# Revit family: Rhoss_WinFLOW_ECO
name_source: partatom
category: Attrezzatura meccanica
units: mm (PartAtom-declared; Revit-internal decimal feet)

## family parameters
Basato su piano di lavoro = No
Condiviso = No
Numero OmniClass = 23.75.00.00
Punto di calcolo locali = No
Quota connettore circolare = Usa diametro
Sempre verticale = Sì
Taglio con vuoti quando caricato = No
Tipo di parte = Normale
Titolo OmniClass = Climate Control (HVAC)

## types (30) — shared parameters
C Ref = R454B
COND_IN_Diametro = 76 mm
COND_IN_R1 = 0.00°
COND_IN_R2 = 0.00°
COND_OUT_Diametro = 76 mm
COND_OUT_R1 = 0.00°
COND_OUT_R2 = 0.00°
DS_IN_Diametro = 38 mm  [stored 0.124672 ft]
DS_IN_R1 = 0.00°
DS_IN_R2 = 0.00°
DS_OUT_Diametro = 38 mm  [stored 0.124672 ft]
DS_OUT_R1 = 0.00°
DS_OUT_R2 = 0.00°
D_Main = 2209 mm  [stored 7.24738 ft]
D_W_Idra = 3434 mm  [stored 11.2664 ft]
DistanzaDivisorio = 750 mm  [stored 2.46063 ft]
DivisorioOrizzontale_01 = Sì
EVAP_IN_B = 1680 mm  [stored 5.51181 ft]
EVAP_IN_C = 650 mm  [stored 2.13255 ft]
EVAP_IN_Diametro = 76 mm
EVAP_IN_R1 = 0.00°
EVAP_IN_R2 = 0.00°
EVAP_OUT_B = 1290 mm  [stored 4.23228 ft]
EVAP_OUT_C = 650 mm  [stored 2.13255 ft]
EVAP_OUT_Diametro = 76 mm
EVAP_OUT_R1 = 0.00°
EVAP_OUT_R2 = 0.00°
FREON_IN_R1 = 0.00°
FREON_IN_R2 = 0.00°
FREON_OUT_R1 = 0.00°
FREON_OUT_R2 = 0.00°
H_Main = 1855 mm  [stored 6.08596 ft]
Immagine tipo = <Nessuno>
LogoVisibilita = Sì
LongFeet = Sì
Produttore = Rhoss spa
QE_H = 1666 mm  [stored 5.46588 ft]
QE_Spessore_esterno = 300 mm  [stored 0.984252 ft]
QE_W = 860 mm  [stored 2.82152 ft]
RAL 9018 = RAL 9018
REC_IN_Diametro = 76 mm
REC_IN_R1 = 0.00°
REC_IN_R2 = 0.00°
REC_OUT_Diametro = 76 mm
REC_OUT_R1 = 0.00°
REC_OUT_R2 = 0.00°
RispettoD1 = 1200 mm  [stored 3.93701 ft]
RispettoD2 = 1000 mm  [stored 3.28084 ft]
RispettoD4 = 1000 mm  [stored 3.28084 ft]
RispettoMateriale = BoxRispetto
Rispetto_H_daTerra = 3000 mm  [stored 9.84252 ft]
ShortFeet = No
URL = www.rhoss.com
VisibManiglia = Sì
W_Main = 870 mm  [stored 2.85433 ft]
zero-valued in all types: Prospetto di default, __, ____, _____, ______, _______, pResC (kPa), pResE (kPa)

## per-type parameters (varying)
- TCHETU 4185: COND_IN_A=200 mm  [stored 0.656168 ft]; COND_IN_B=350 mm  [stored 1.14829 ft]; COND_IN_C=150 mm  [stored 0.492126 ft]; COND_IN_R3=0.00°; COND_OUT_A=200 mm  [stored 0.656168 ft]; COND_OUT_B=350 mm  [stored 1.14829 ft]; COND_OUT_C=200 mm  [stored 0.656168 ft]; COND_OUT_R3=0.00°; COP_EN14511_W7W45=0; DS_IN_A=200 mm  [stored 0.656168 ft]; DS_IN_B=475 mm  [stored 1.5584 ft]; DS_IN_C=204 mm  [stored 0.669291 ft]; DS_IN_R3=0.00°; DS_OUT_A=200 mm  [stored 0.656168 ft]; DS_OUT_B=725 mm  [stored 2.37861 ft]; DS_OUT_C=204 mm  [stored 0.669291 ft]; DS_OUT_R3=0.00°; EER_EN14511_W35W7=0; EER_EN14511_tC50W7=0; EVAP_IN_A=200 mm  [stored 0.656168 ft]; EVAP_IN_R3=0.00°; EVAP_OUT_A=200 mm  [stored 0.656168 ft]; EVAP_OUT_R3=0.00°; FREON_IN_A=200 mm  [stored 0.656168 ft]; FREON_IN_B=1290 mm  [stored 4.23228 ft]; FREON_IN_C=220 mm  [stored 0.721785 ft]; FREON_IN_Diametro=22 mm  [stored 0.0721785 ft]; FREON_IN_R3=0.00°; FREON_OUT_A=200 mm  [stored 0.656168 ft]; FREON_OUT_B=1680 mm  [stored 5.51181 ft]; FREON_OUT_C=220 mm  [stored 0.721785 ft]; FREON_OUT_Diametro=35 mm  [stored 0.114829 ft]; FREON_OUT_R3=0.00°; F_Mid_STR6=1699 mm; F_OffSet=491 mm  [stored 1.61089 ft]; Frequency (Hz)=0; Is_STR5=No; Is_STR6=Sì; Lw (dBA)=79; Maximum current (A)=0; Nominal current (A)=0; PF_EN14511_W35W7 (kW)=0; PF_EN14511_tC50W7 (kW)=0; PR_EN14511_W45 (kW)=0; PT_EN14511_W7W45 (kW)=0; Psm_EN14511_W35W7 (kW)=0; QTc (m3/h)=0; Qc (m3/h)=0; Qe (m3/h)=0; Qr (m3/h)=0; REC_IN_A=200 mm  [stored 0.656168 ft]; REC_IN_B=475 mm  [stored 1.5584 ft]; REC_IN_C=220 mm  [stored 0.721785 ft]; REC_IN_R3=0.00°; REC_OUT_A=200 mm  [stored 0.656168 ft]; REC_OUT_B=865 mm  [stored 2.83793 ft]; REC_OUT_C=220 mm  [stored 0.721785 ft]; REC_OUT_R3=0.00°; RispettoD3=3434 mm  [stored 11.2664 ft]; SCOP_EN14825=0; SEER_EN14825=0; Starting current (A)=0; Type=CHILLER; Voltage (V)=0; Weight (kg)=1040; dPTc (kPa)=0; dPc (kPa)=0; dPe (kPa)=0; dPr (kPa)=0; n. poles=0
- TCHETU 4210: COND_IN_A=2209 mm  [stored 7.24738 ft]; COND_IN_B=1290 mm  [stored 4.23228 ft]; COND_IN_C=220 mm  [stored 0.721785 ft]; COND_IN_R3=269.98°; COND_OUT_A=2209 mm  [stored 7.24738 ft]; COND_OUT_B=1680 mm  [stored 5.51181 ft]; COND_OUT_C=220 mm  [stored 0.721785 ft]; COND_OUT_R3=269.98°; COP_EN14511_W7W45=0; DS_IN_A=2209 mm  [stored 7.24738 ft]; DS_IN_B=475 mm  [stored 1.5584 ft]; DS_IN_C=204 mm  [stored 0.669291 ft]; DS_IN_R3=269.98°; DS_OUT_A=2209 mm  [stored 7.24738 ft]; DS_OUT_B=725 mm  [stored 2.37861 ft]; DS_OUT_C=204 mm  [stored 0.669291 ft]; DS_OUT_R3=269.98°; EER_EN14511_W35W7=4.62; EER_EN14511_tC50W7=0; EVAP_IN_A=2209 mm  [stored 7.24738 ft]; EVAP_IN_R3=269.98°; EVAP_OUT_A=2209 mm  [stored 7.24738 ft]; EVAP_OUT_R3=269.98°; FREON_IN_A=200 mm  [stored 0.656168 ft]; FREON_IN_B=300 mm  [stored 0.984252 ft]; FREON_IN_C=150 mm  [stored 0.492126 ft]; FREON_IN_Diametro=22 mm  [stored 0.0721785 ft]; FREON_IN_R3=0.00°; FREON_OUT_A=200 mm  [stored 0.656168 ft]; FREON_OUT_B=300 mm  [stored 0.984252 ft]; FREON_OUT_C=200 mm  [stored 0.656168 ft]; FREON_OUT_Diametro=35 mm  [stored 0.114829 ft]; FREON_OUT_R3=0.00°; F_Mid_STR6=795 mm  [stored 2.60827 ft]; F_OffSet=255 mm  [stored 0.836614 ft]; Frequency (Hz)=50; Is_STR5=Sì; Is_STR6=No; Lw (dBA)=79; Maximum current (A)=128.8; Nominal current (A)=81; PF_EN14511_W35W7 (kW)=209; PF_EN14511_tC50W7 (kW)=0; PR_EN14511_W45 (kW)=0; PT_EN14511_W7W45 (kW)=0; Psm_EN14511_W35W7 (kW)=251.4; QTc (m3/h)=0; Qc (m3/h)=43.2; Qe (m3/h)=36; Qr (m3/h)=0; REC_IN_A=2209 mm  [stored 7.24738 ft]; REC_IN_B=475 mm  [stored 1.5584 ft]; REC_IN_C=220 mm  [stored 0.721785 ft]; REC_IN_R3=269.98°; REC_OUT_A=2209 mm  [stored 7.24738 ft]; REC_OUT_B=865 mm  [stored 2.83793 ft]; REC_OUT_C=220 mm  [stored 0.721785 ft]; REC_OUT_R3=269.98°; RispettoD3=2209 mm  [stored 7.24738 ft]; SCOP_EN14825=0; SEER_EN14825=6.36; Starting current (A)=302.4; Type=CHILLER; Voltage (V)=400; Weight (kg)=1105; dPTc (kPa)=0; dPc (kPa)=49; dPe (kPa)=34; dPr (kPa)=0; n. poles=3+N
- TCHETU 4240: COND_IN_A=2209 mm  [stored 7.24738 ft]; COND_IN_B=1290 mm  [stored 4.23228 ft]; COND_IN_C=220 mm  [stored 0.721785 ft]; COND_IN_R3=269.98°; COND_OUT_A=2209 mm  [stored 7.24738 ft]; COND_OUT_B=1680 mm  [stored 5.51181 ft]; COND_OUT_C=220 mm  [stored 0.721785 ft]; COND_OUT_R3=269.98°; COP_EN14511_W7W45=0; DS_IN_A=2209 mm  [stored 7.24738 ft]; DS_IN_B=475 mm  [stored 1.5584 ft]; DS_IN_C=204 mm  [stored 0.669291 ft]; DS_IN_R3=269.98°; DS_OUT_A=2209 mm  [stored 7.24738 ft]; DS_OUT_B=725 mm  [stored 2.37861 ft]; DS_OUT_C=204 mm  [stored 0.669291 ft]; DS_OUT_R3=269.98°; EER_EN14511_W35W7=4.63; EER_EN14511_tC50W7=0; EVAP_IN_A=2209 mm  [stored 7.24738 ft]; EVAP_IN_R3=269.98°; EVAP_OUT_A=2209 mm  [stored 7.24738 ft]; EVAP_OUT_R3=269.98°; FREON_IN_A=200 mm  [stored 0.656168 ft]; FREON_IN_B=300 mm  [stored 0.984252 ft]; FREON_IN_C=150 mm  [stored 0.492126 ft]; FREON_IN_Diametro=22 mm  [stored 0.0721785 ft]; FREON_IN_R3=0.00°; FREON_OUT_A=200 mm  [stored 0.656168 ft]; FREON_OUT_B=300 mm  [stored 0.984252 ft]; FREON_OUT_C=200 mm  [stored 0.656168 ft]; FREON_OUT_Diametro=35 mm  [stored 0.114829 ft]; FREON_OUT_R3=0.00°; F_Mid_STR6=795 mm  [stored 2.60827 ft]; F_OffSet=255 mm  [stored 0.836614 ft]; Frequency (Hz)=50; Is_STR5=Sì; Is_STR6=No; Lw (dBA)=80; Maximum current (A)=149.6; Nominal current (A)=94.4; PF_EN14511_W35W7 (kW)=236.3; PF_EN14511_tC50W7 (kW)=0; PR_EN14511_W45 (kW)=0; PT_EN14511_W7W45 (kW)=0; Psm_EN14511_W35W7 (kW)=284.4; QTc (m3/h)=0; Qc (m3/h)=48.9; Qe (m3/h)=40.7; Qr (m3/h)=0; REC_IN_A=2209 mm  [stored 7.24738 ft]; REC_IN_B=475 mm  [stored 1.5584 ft]; REC_IN_C=220 mm  [stored 0.721785 ft]; REC_IN_R3=269.98°; REC_OUT_A=2209 mm  [stored 7.24738 ft]; REC_OUT_B=865 mm  [stored 2.83793 ft]; REC_OUT_C=220 mm  [stored 0.721785 ft]; REC_OUT_R3=269.98°; RispettoD3=2209 mm  [stored 7.24738 ft]; SCOP_EN14825=0; SEER_EN14825=6.5; Starting current (A)=323.2; Type=CHILLER; Voltage (V)=400; Weight (kg)=1140; dPTc (kPa)=0; dPc (kPa)=42; dPe (kPa)=29; dPr (kPa)=0; n. poles=3+N
- TCHETU 4275: COND_IN_A=2209 mm  [stored 7.24738 ft]; COND_IN_B=1290 mm  [stored 4.23228 ft]; COND_IN_C=220 mm  [stored 0.721785 ft]; COND_IN_R3=269.98°; COND_OUT_A=2209 mm  [stored 7.24738 ft]; COND_OUT_B=1680 mm  [stored 5.51181 ft]; COND_OUT_C=220 mm  [stored 0.721785 ft]; COND_OUT_R3=269.98°; COP_EN14511_W7W45=0; DS_IN_A=2209 mm  [stored 7.24738 ft]; DS_IN_B=475 mm  [stored 1.5584 ft]; DS_IN_C=204 mm  [stored 0.669291 ft]; DS_IN_R3=269.98°; DS_OUT_A=2209 mm  [stored 7.24738 ft]; DS_OUT_B=725 mm  [stored 2.37861 ft]; DS_OUT_C=204 mm  [stored 0.669291 ft]; DS_OUT_R3=269.98°; EER_EN14511_W35W7=4.59; EER_EN14511_tC50W7=0; EVAP_IN_A=2209 mm  [stored 7.24738 ft]; EVAP_IN_R3=269.98°; EVAP_OUT_A=2209 mm  [stored 7.24738 ft]; EVAP_OUT_R3=269.98°; FREON_IN_A=200 mm  [stored 0.656168 ft]; FREON_IN_B=300 mm  [stored 0.984252 ft]; FREON_IN_C=150 mm  [stored 0.492126 ft]; FREON_IN_Diametro=22 mm  [stored 0.0721785 ft]; FREON_IN_R3=0.00°; FREON_OUT_A=200 mm  [stored 0.656168 ft]; FREON_OUT_B=300 mm  [stored 0.984252 ft]; FREON_OUT_C=200 mm  [stored 0.656168 ft]; FREON_OUT_Diametro=35 mm  [stored 0.114829 ft]; FREON_OUT_R3=0.00°; F_Mid_STR6=795 mm  [stored 2.60827 ft]; F_OffSet=255 mm  [stored 0.836614 ft]; Frequency (Hz)=50; Is_STR5=Sì; Is_STR6=No; Lw (dBA)=81; Maximum current (A)=166.4; Nominal current (A)=97.3; PF_EN14511_W35W7 (kW)=267.9; PF_EN14511_tC50W7 (kW)=0; PR_EN14511_W45 (kW)=0; PT_EN14511_W7W45 (kW)=0; Psm_EN14511_W35W7 (kW)=322.5; QTc (m3/h)=0; Qc (m3/h)=55.5; Qe (m3/h)=46.1; Qr (m3/h)=0; REC_IN_A=2209 mm  [stored 7.24738 ft]; REC_IN_B=475 mm  [stored 1.5584 ft]; REC_IN_C=220 mm  [stored 0.721785 ft]; REC_IN_R3=269.98°; REC_OUT_A=2209 mm  [stored 7.24738 ft]; REC_OUT_B=865 mm  [stored 2.83793 ft]; REC_OUT_C=220 mm  [stored 0.721785 ft]; REC_OUT_R3=269.98°; RispettoD3=2209 mm  [stored 7.24738 ft]; SCOP_EN14825=0; SEER_EN14825=6.49; Starting current (A)=330.6; Type=CHILLER; Voltage (V)=400; Weight (kg)=1310; dPTc (kPa)=0; dPc (kPa)=55; dPe (kPa)=38; dPr (kPa)=0; n. poles=3+N
- TCHETU 4305: COND_IN_A=2209 mm  [stored 7.24738 ft]; COND_IN_B=1290 mm  [stored 4.23228 ft]; COND_IN_C=220 mm  [stored 0.721785 ft]; COND_IN_R3=269.98°; COND_OUT_A=2209 mm  [stored 7.24738 ft]; COND_OUT_B=1680 mm  [stored 5.51181 ft]; COND_OUT_C=220 mm  [stored 0.721785 ft]; COND_OUT_R3=269.98°; COP_EN14511_W7W45=0; DS_IN_A=2209 mm  [stored 7.24738 ft]; DS_IN_B=475 mm  [stored 1.5584 ft]; DS_IN_C=204 mm  [stored 0.669291 ft]; DS_IN_R3=269.98°; DS_OUT_A=2209 mm  [stored 7.24738 ft]; DS_OUT_B=725 mm  [stored 2.37861 ft]; DS_OUT_C=204 mm  [stored 0.669291 ft]; DS_OUT_R3=269.98°; EER_EN14511_W35W7=4.54; EER_EN14511_tC50W7=0; EVAP_IN_A=2209 mm  [stored 7.24738 ft]; EVAP_IN_R3=269.98°; EVAP_OUT_A=2209 mm  [stored 7.24738 ft]; EVAP_OUT_R3=269.98°; FREON_IN_A=200 mm  [stored 0.656168 ft]; FREON_IN_B=300 mm  [stored 0.984252 ft]; FREON_IN_C=150 mm  [stored 0.492126 ft]; FREON_IN_Diametro=22 mm  [stored 0.0721785 ft]; FREON_IN_R3=0.00°; FREON_OUT_A=200 mm  [stored 0.656168 ft]; FREON_OUT_B=300 mm  [stored 0.984252 ft]; FREON_OUT_C=200 mm  [stored 0.656168 ft]; FREON_OUT_Diametro=35 mm  [stored 0.114829 ft]; FREON_OUT_R3=0.00°; F_Mid_STR6=795 mm  [stored 2.60827 ft]; F_OffSet=255 mm  [stored 0.836614 ft]; Frequency (Hz)=50; Is_STR5=Sì; Is_STR6=No; Lw (dBA)=83; Maximum current (A)=183.2; Nominal current (A)=100.4; PF_EN14511_W35W7 (kW)=299.1; PF_EN14511_tC50W7 (kW)=0; PR_EN14511_W45 (kW)=0; PT_EN14511_W7W45 (kW)=0; Psm_EN14511_W35W7 (kW)=360.4; QTc (m3/h)=0; Qc (m3/h)=62; Qe (m3/h)=51.5; Qr (m3/h)=0; REC_IN_A=2209 mm  [stored 7.24738 ft]; REC_IN_B=475 mm  [stored 1.5584 ft]; REC_IN_C=220 mm  [stored 0.721785 ft]; REC_IN_R3=269.98°; REC_OUT_A=2209 mm  [stored 7.24738 ft]; REC_OUT_B=865 mm  [stored 2.83793 ft]; REC_OUT_C=220 mm  [stored 0.721785 ft]; REC_OUT_R3=269.98°; RispettoD3=2209 mm  [stored 7.24738 ft]; SCOP_EN14825=0; SEER_EN14825=6.56; Starting current (A)=347.4; Type=CHILLER; Voltage (V)=400; Weight (kg)=1455; dPTc (kPa)=0; dPc (kPa)=68; dPe (kPa)=47; dPr (kPa)=0; n. poles=3+N
- TCHETU 4350: COND_IN_A=2209 mm  [stored 7.24738 ft]; COND_IN_B=1290 mm  [stored 4.23228 ft]; COND_IN_C=220 mm  [stored 0.721785 ft]; COND_IN_R3=269.98°; COND_OUT_A=2209 mm  [stored 7.24738 ft]; COND_OUT_B=1680 mm  [stored 5.51181 ft]; COND_OUT_C=220 mm  [stored 0.721785 ft]; COND_OUT_R3=269.98°; COP_EN14511_W7W45=0; DS_IN_A=2209 mm  [stored 7.24738 ft]; DS_IN_B=475 mm  [stored 1.5584 ft]; DS_IN_C=204 mm  [stored 0.669291 ft]; DS_IN_R3=269.98°; DS_OUT_A=2209 mm  [stored 7.24738 ft]; DS_OUT_B=725 mm  [stored 2.37861 ft]; DS_OUT_C=204 mm  [stored 0.669291 ft]; DS_OUT_R3=269.98°; EER_EN14511_W35W7=4.54; EER_EN14511_tC50W7=0; EVAP_IN_A=2209 mm  [stored 7.24738 ft]; EVAP_IN_R3=269.98°; EVAP_OUT_A=2209 mm  [stored 7.24738 ft]; EVAP_OUT_R3=269.98°; FREON_IN_A=200 mm  [stored 0.656168 ft]; FREON_IN_B=300 mm  [stored 0.984252 ft]; FREON_IN_C=150 mm  [stored 0.492126 ft]; FREON_IN_Diametro=22 mm  [stored 0.0721785 ft]; FREON_IN_R3=0.00°; FREON_OUT_A=200 mm  [stored 0.656168 ft]; FREON_OUT_B=300 mm  [stored 0.984252 ft]; FREON_OUT_C=200 mm  [stored 0.656168 ft]; FREON_OUT_Diametro=35 mm  [stored 0.114829 ft]; FREON_OUT_R3=0.00°; F_Mid_STR6=795 mm  [stored 2.60827 ft]; F_OffSet=255 mm  [stored 0.836614 ft]; Frequency (Hz)=50; Is_STR5=Sì; Is_STR6=No; Lw (dBA)=84; Maximum current (A)=216.4; Nominal current (A)=125; PF_EN14511_W35W7 (kW)=344; PF_EN14511_tC50W7 (kW)=0; PR_EN14511_W45 (kW)=0; PT_EN14511_W7W45 (kW)=0; Psm_EN14511_W35W7 (kW)=414.6; QTc (m3/h)=0; Qc (m3/h)=71.3; Qe (m3/h)=59.2; Qr (m3/h)=0; REC_IN_A=2209 mm  [stored 7.24738 ft]; REC_IN_B=475 mm  [stored 1.5584 ft]; REC_IN_C=220 mm  [stored 0.721785 ft]; REC_IN_R3=269.98°; REC_OUT_A=2209 mm  [stored 7.24738 ft]; REC_OUT_B=865 mm  [stored 2.83793 ft]; REC_OUT_C=220 mm  [stored 0.721785 ft]; REC_OUT_R3=269.98°; RispettoD3=2209 mm  [stored 7.24738 ft]; SCOP_EN14825=0; SEER_EN14825=6.54; Starting current (A)=480; Type=CHILLER; Voltage (V)=400; Weight (kg)=1515; dPTc (kPa)=0; dPc (kPa)=64; dPe (kPa)=44; dPr (kPa)=0; n. poles=3+N
- TCHETU 4395: COND_IN_A=2209 mm  [stored 7.24738 ft]; COND_IN_B=1290 mm  [stored 4.23228 ft]; COND_IN_C=220 mm  [stored 0.721785 ft]; COND_IN_R3=269.98°; COND_OUT_A=2209 mm  [stored 7.24738 ft]; COND_OUT_B=1680 mm  [stored 5.51181 ft]; COND_OUT_C=220 mm  [stored 0.721785 ft]; COND_OUT_R3=269.98°; COP_EN14511_W7W45=0; DS_IN_A=2209 mm  [stored 7.24738 ft]; DS_IN_B=475 mm  [stored 1.5584 ft]; DS_IN_C=204 mm  [stored 0.669291 ft]; DS_IN_R3=269.98°; DS_OUT_A=2209 mm  [stored 7.24738 ft]; DS_OUT_B=725 mm  [stored 2.37861 ft]; DS_OUT_C=204 mm  [stored 0.669291 ft]; DS_OUT_R3=269.98°; EER_EN14511_W35W7=4.44; EER_EN14511_tC50W7=0; EVAP_IN_A=2209 mm  [stored 7.24738 ft]; EVAP_IN_R3=269.98°; EVAP_OUT_A=2209 mm  [stored 7.24738 ft]; EVAP_OUT_R3=269.98°; FREON_IN_A=200 mm  [stored 0.656168 ft]; FREON_IN_B=300 mm  [stored 0.984252 ft]; FREON_IN_C=150 mm  [stored 0.492126 ft]; FREON_IN_Diametro=22 mm  [stored 0.0721785 ft]; FREON_IN_R3=0.00°; FREON_OUT_A=200 mm  [stored 0.656168 ft]; FREON_OUT_B=300 mm  [stored 0.984252 ft]; FREON_OUT_C=200 mm  [stored 0.656168 ft]; FREON_OUT_Diametro=35 mm  [stored 0.114829 ft]; FREON_OUT_R3=0.00°; F_Mid_STR6=795 mm  [stored 2.60827 ft]; F_OffSet=255 mm  [stored 0.836614 ft]; Frequency (Hz)=50; Is_STR5=Sì; Is_STR6=No; Lw (dBA)=85; Maximum current (A)=249.6; Nominal current (A)=151.2; PF_EN14511_W35W7 (kW)=387.6; PF_EN14511_tC50W7 (kW)=0; PR_EN14511_W45 (kW)=0; PT_EN14511_W7W45 (kW)=0; Psm_EN14511_W35W7 (kW)=468.5; QTc (m3/h)=0; Qc (m3/h)=80.6; Qe (m3/h)=66.8; Qr (m3/h)=0; REC_IN_A=2209 mm  [stored 7.24738 ft]; REC_IN_B=475 mm  [stored 1.5584 ft]; REC_IN_C=220 mm  [stored 0.721785 ft]; REC_IN_R3=269.98°; REC_OUT_A=2209 mm  [stored 7.24738 ft]; REC_OUT_B=865 mm  [stored 2.83793 ft]; REC_OUT_C=220 mm  [stored 0.721785 ft]; REC_OUT_R3=269.98°; RispettoD3=2209 mm  [stored 7.24738 ft]; SCOP_EN14825=0; SEER_EN14825=6.6; Starting current (A)=513.2; Type=CHILLER; Voltage (V)=400; Weight (kg)=1530; dPTc (kPa)=0; dPc (kPa)=79; dPe (kPa)=54; dPr (kPa)=0; n. poles=3+N
- THHETU 4185: COND_IN_A=2209 mm  [stored 7.24738 ft]; COND_IN_B=1290 mm  [stored 4.23228 ft]; COND_IN_C=220 mm  [stored 0.721785 ft]; COND_IN_R3=269.98°; COND_OUT_A=2209 mm  [stored 7.24738 ft]; COND_OUT_B=1680 mm  [stored 5.51181 ft]; COND_OUT_C=220 mm  [stored 0.721785 ft]; COND_OUT_R3=269.98°; COP_EN14511_W7W45=4.27; DS_IN_A=2209 mm  [stored 7.24738 ft]; DS_IN_B=475 mm  [stored 1.5584 ft]; DS_IN_C=204 mm  [stored 0.669291 ft]; DS_IN_R3=269.98°; DS_OUT_A=2209 mm  [stored 7.24738 ft]; DS_OUT_B=725 mm  [stored 2.37861 ft]; DS_OUT_C=204 mm  [stored 0.669291 ft]; DS_OUT_R3=269.98°; EER_EN14511_W35W7=4.6; EER_EN14511_tC50W7=0; EVAP_IN_A=2209 mm  [stored 7.24738 ft]; EVAP_IN_R3=269.98°; EVAP_OUT_A=2209 mm  [stored 7.24738 ft]; EVAP_OUT_R3=269.98°; FREON_IN_A=200 mm  [stored 0.656168 ft]; FREON_IN_B=300 mm  [stored 0.984252 ft]; FREON_IN_C=150 mm  [stored 0.492126 ft]; FREON_IN_Diametro=22 mm  [stored 0.0721785 ft]; FREON_IN_R3=0.00°; FREON_OUT_A=200 mm  [stored 0.656168 ft]; FREON_OUT_B=300 mm  [stored 0.984252 ft]; FREON_OUT_C=200 mm  [stored 0.656168 ft]; FREON_OUT_Diametro=35 mm  [stored 0.114829 ft]; FREON_OUT_R3=0.00°; F_Mid_STR6=795 mm  [stored 2.60827 ft]; F_OffSet=255 mm  [stored 0.836614 ft]; Frequency (Hz)=50; Is_STR5=Sì; Is_STR6=No; Lw (dBA)=79; Maximum current (A)=108; Nominal current (A)=68.1; PF_EN14511_W35W7 (kW)=180.2; PF_EN14511_tC50W7 (kW)=0; PR_EN14511_W45 (kW)=0; PT_EN14511_W7W45 (kW)=205.4; Psm_EN14511_W35W7 (kW)=217.2; QTc (m3/h)=35.3; Qc (m3/h)=37.4; Qe (m3/h)=31; Qr (m3/h)=0; REC_IN_A=200 mm  [stored 0.656168 ft]; REC_IN_B=250 mm  [stored 0.82021 ft]; REC_IN_C=250 mm  [stored 0.82021 ft]; REC_IN_R3=0.00°; REC_OUT_A=200 mm  [stored 0.656168 ft]; REC_OUT_B=300 mm  [stored 0.984252 ft]; REC_OUT_C=250 mm  [stored 0.82021 ft]; REC_OUT_R3=0.00°; RispettoD3=2209 mm  [stored 7.24738 ft]; SCOP_EN14825=6.93; SEER_EN14825=6.09; Starting current (A)=253; Type=HEAT PUMP; Voltage (V)=400; Weight (kg)=1125; dPTc (kPa)=34; dPc (kPa)=38; dPe (kPa)=26; dPr (kPa)=0; n. poles=3+N
- THHETU 4210: COND_IN_A=2209 mm  [stored 7.24738 ft]; COND_IN_B=1290 mm  [stored 4.23228 ft]; COND_IN_C=220 mm  [stored 0.721785 ft]; COND_IN_R3=269.98°; COND_OUT_A=2209 mm  [stored 7.24738 ft]; COND_OUT_B=1680 mm  [stored 5.51181 ft]; COND_OUT_C=220 mm  [stored 0.721785 ft]; COND_OUT_R3=269.98°; COP_EN14511_W7W45=4.19; DS_IN_A=2209 mm  [stored 7.24738 ft]; DS_IN_B=475 mm  [stored 1.5584 ft]; DS_IN_C=204 mm  [stored 0.669291 ft]; DS_IN_R3=269.98°; DS_OUT_A=2209 mm  [stored 7.24738 ft]; DS_OUT_B=725 mm  [stored 2.37861 ft]; DS_OUT_C=204 mm  [stored 0.669291 ft]; DS_OUT_R3=269.98°; EER_EN14511_W35W7=4.47; EER_EN14511_tC50W7=0; EVAP_IN_A=2209 mm  [stored 7.24738 ft]; EVAP_IN_R3=269.98°; EVAP_OUT_A=2209 mm  [stored 7.24738 ft]; EVAP_OUT_R3=269.98°; FREON_IN_A=200 mm  [stored 0.656168 ft]; FREON_IN_B=300 mm  [stored 0.984252 ft]; FREON_IN_C=150 mm  [stored 0.492126 ft]; FREON_IN_Diametro=22 mm  [stored 0.0721785 ft]; FREON_IN_R3=0.00°; FREON_OUT_A=200 mm  [stored 0.656168 ft]; FREON_OUT_B=300 mm  [stored 0.984252 ft]; FREON_OUT_C=200 mm  [stored 0.656168 ft]; FREON_OUT_Diametro=35 mm  [stored 0.114829 ft]; FREON_OUT_R3=0.00°; F_Mid_STR6=795 mm  [stored 2.60827 ft]; F_OffSet=255 mm  [stored 0.836614 ft]; Frequency (Hz)=50; Is_STR5=Sì; Is_STR6=No; Lw (dBA)=79; Maximum current (A)=128.8; Nominal current (A)=82.8; PF_EN14511_W35W7 (kW)=206.3; PF_EN14511_tC50W7 (kW)=0; PR_EN14511_W45 (kW)=0; PT_EN14511_W7W45 (kW)=237.4; Psm_EN14511_W35W7 (kW)=249.7; QTc (m3/h)=40.8; Qc (m3/h)=42.9; Qe (m3/h)=35.5; Qr (m3/h)=0; REC_IN_A=200 mm  [stored 0.656168 ft]; REC_IN_B=250 mm  [stored 0.82021 ft]; REC_IN_C=250 mm  [stored 0.82021 ft]; REC_IN_R3=0.00°; REC_OUT_A=200 mm  [stored 0.656168 ft]; REC_OUT_B=300 mm  [stored 0.984252 ft]; REC_OUT_C=250 mm  [stored 0.82021 ft]; REC_OUT_R3=0.00°; RispettoD3=2209 mm  [stored 7.24738 ft]; SCOP_EN14825=6.79; SEER_EN14825=6.1; Starting current (A)=302.4; Type=HEAT PUMP; Voltage (V)=400; Weight (kg)=1135; dPTc (kPa)=43; dPc (kPa)=48; dPe (kPa)=33; dPr (kPa)=0; n. poles=3+N
- THHETU 4240: COND_IN_A=2209 mm  [stored 7.24738 ft]; COND_IN_B=1290 mm  [stored 4.23228 ft]; COND_IN_C=220 mm  [stored 0.721785 ft]; COND_IN_R3=269.98°; COND_OUT_A=2209 mm  [stored 7.24738 ft]; COND_OUT_B=1680 mm  [stored 5.51181 ft]; COND_OUT_C=220 mm  [stored 0.721785 ft]; COND_OUT_R3=269.98°; COP_EN14511_W7W45=4.2; DS_IN_A=2209 mm  [stored 7.24738 ft]; DS_IN_B=475 mm  [stored 1.5584 ft]; DS_IN_C=204 mm  [stored 0.669291 ft]; DS_IN_R3=269.98°; DS_OUT_A=2209 mm  [stored 7.24738 ft]; DS_OUT_B=725 mm  [stored 2.37861 ft]; DS_OUT_C=204 mm  [stored 0.669291 ft]; DS_OUT_R3=269.98°; EER_EN14511_W35W7=4.46; EER_EN14511_tC50W7=0; EVAP_IN_A=2209 mm  [stored 7.24738 ft]; EVAP_IN_R3=269.98°; EVAP_OUT_A=2209 mm  [stored 7.24738 ft]; EVAP_OUT_R3=269.98°; FREON_IN_A=200 mm  [stored 0.656168 ft]; FREON_IN_B=300 mm  [stored 0.984252 ft]; FREON_IN_C=150 mm  [stored 0.492126 ft]; FREON_IN_Diametro=22 mm  [stored 0.0721785 ft]; FREON_IN_R3=0.00°; FREON_OUT_A=200 mm  [stored 0.656168 ft]; FREON_OUT_B=300 mm  [stored 0.984252 ft]; FREON_OUT_C=200 mm  [stored 0.656168 ft]; FREON_OUT_Diametro=35 mm  [stored 0.114829 ft]; FREON_OUT_R3=0.00°; F_Mid_STR6=795 mm  [stored 2.60827 ft]; F_OffSet=255 mm  [stored 0.836614 ft]; Frequency (Hz)=50; Is_STR5=Sì; Is_STR6=No; Lw (dBA)=80; Maximum current (A)=149.6; Nominal current (A)=96.5; PF_EN14511_W35W7 (kW)=232.6; PF_EN14511_tC50W7 (kW)=0; PR_EN14511_W45 (kW)=0; PT_EN14511_W7W45 (kW)=268.2; Psm_EN14511_W35W7 (kW)=281.8; QTc (m3/h)=46.1; Qc (m3/h)=48.5; Qe (m3/h)=40.1; Qr (m3/h)=0; REC_IN_A=200 mm  [stored 0.656168 ft]; REC_IN_B=250 mm  [stored 0.82021 ft]; REC_IN_C=250 mm  [stored 0.82021 ft]; REC_IN_R3=0.00°; REC_OUT_A=200 mm  [stored 0.656168 ft]; REC_OUT_B=300 mm  [stored 0.984252 ft]; REC_OUT_C=250 mm  [stored 0.82021 ft]; REC_OUT_R3=0.00°; RispettoD3=2209 mm  [stored 7.24738 ft]; SCOP_EN14825=6.69; SEER_EN14825=6.26; Starting current (A)=323.2; Type=HEAT PUMP; Voltage (V)=400; Weight (kg)=1180; dPTc (kPa)=38; dPc (kPa)=42; dPe (kPa)=29; dPr (kPa)=0; n. poles=3+N
- THHETU 4275: COND_IN_A=2209 mm  [stored 7.24738 ft]; COND_IN_B=1290 mm  [stored 4.23228 ft]; COND_IN_C=220 mm  [stored 0.721785 ft]; COND_IN_R3=269.98°; COND_OUT_A=2209 mm  [stored 7.24738 ft]; COND_OUT_B=1680 mm  [stored 5.51181 ft]; COND_OUT_C=220 mm  [stored 0.721785 ft]; COND_OUT_R3=269.98°; COP_EN14511_W7W45=4.1; DS_IN_A=2209 mm  [stored 7.24738 ft]; DS_IN_B=475 mm  [stored 1.5584 ft]; DS_IN_C=204 mm  [stored 0.669291 ft]; DS_IN_R3=269.98°; DS_OUT_A=2209 mm  [stored 7.24738 ft]; DS_OUT_B=725 mm  [stored 2.37861 ft]; DS_OUT_C=204 mm  [stored 0.669291 ft]; DS_OUT_R3=269.98°; EER_EN14511_W35W7=4.4; EER_EN14511_tC50W7=0; EVAP_IN_A=2209 mm  [stored 7.24738 ft]; EVAP_IN_R3=269.98°; EVAP_OUT_A=2209 mm  [stored 7.24738 ft]; EVAP_OUT_R3=269.98°; FREON_IN_A=200 mm  [stored 0.656168 ft]; FREON_IN_B=300 mm  [stored 0.984252 ft]; FREON_IN_C=150 mm  [stored 0.492126 ft]; FREON_IN_Diametro=22 mm  [stored 0.0721785 ft]; FREON_IN_R3=0.00°; FREON_OUT_A=200 mm  [stored 0.656168 ft]; FREON_OUT_B=300 mm  [stored 0.984252 ft]; FREON_OUT_C=200 mm  [stored 0.656168 ft]; FREON_OUT_Diametro=35 mm  [stored 0.114829 ft]; FREON_OUT_R3=0.00°; F_Mid_STR6=795 mm  [stored 2.60827 ft]; F_OffSet=255 mm  [stored 0.836614 ft]; Frequency (Hz)=50; Is_STR5=Sì; Is_STR6=No; Lw (dBA)=81; Maximum current (A)=166.4; Nominal current (A)=99.6; PF_EN14511_W35W7 (kW)=262.2; PF_EN14511_tC50W7 (kW)=0; PR_EN14511_W45 (kW)=0; PT_EN14511_W7W45 (kW)=303.7; Psm_EN14511_W35W7 (kW)=318.1; QTc (m3/h)=52.2; Qc (m3/h)=54.7; Qe (m3/h)=45.2; Qr (m3/h)=0; REC_IN_A=200 mm  [stored 0.656168 ft]; REC_IN_B=250 mm  [stored 0.82021 ft]; REC_IN_C=250 mm  [stored 0.82021 ft]; REC_IN_R3=0.00°; REC_OUT_A=200 mm  [stored 0.656168 ft]; REC_OUT_B=300 mm  [stored 0.984252 ft]; REC_OUT_C=250 mm  [stored 0.82021 ft]; REC_OUT_R3=0.00°; RispettoD3=2209 mm  [stored 7.24738 ft]; SCOP_EN14825=6.63; SEER_EN14825=6.25; Starting current (A)=330.6; Type=HEAT PUMP; Voltage (V)=400; Weight (kg)=1360; dPTc (kPa)=48; dPc (kPa)=53; dPe (kPa)=36; dPr (kPa)=0; n. poles=3+N
- THHETU 4305: COND_IN_A=2209 mm  [stored 7.24738 ft]; COND_IN_B=1290 mm  [stored 4.23228 ft]; COND_IN_C=220 mm  [stored 0.721785 ft]; COND_IN_R3=269.98°; COND_OUT_A=2209 mm  [stored 7.24738 ft]; COND_OUT_B=1680 mm  [stored 5.51181 ft]; COND_OUT_C=220 mm  [stored 0.721785 ft]; COND_OUT_R3=269.98°; COP_EN14511_W7W45=3.98; DS_IN_A=2209 mm  [stored 7.24738 ft]; DS_IN_B=475 mm  [stored 1.5584 ft]; DS_IN_C=204 mm  [stored 0.669291 ft]; DS_IN_R3=269.98°; DS_OUT_A=2209 mm  [stored 7.24738 ft]; DS_OUT_B=725 mm  [stored 2.37861 ft]; DS_OUT_C=204 mm  [stored 0.669291 ft]; DS_OUT_R3=269.98°; EER_EN14511_W35W7=4.35; EER_EN14511_tC50W7=0; EVAP_IN_A=2209 mm  [stored 7.24738 ft]; EVAP_IN_R3=269.98°; EVAP_OUT_A=2209 mm  [stored 7.24738 ft]; EVAP_OUT_R3=269.98°; FREON_IN_A=200 mm  [stored 0.656168 ft]; FREON_IN_B=300 mm  [stored 0.984252 ft]; FREON_IN_C=150 mm  [stored 0.492126 ft]; FREON_IN_Diametro=22 mm  [stored 0.0721785 ft]; FREON_IN_R3=0.00°; FREON_OUT_A=200 mm  [stored 0.656168 ft]; FREON_OUT_B=300 mm  [stored 0.984252 ft]; FREON_OUT_C=200 mm  [stored 0.656168 ft]; FREON_OUT_Diametro=35 mm  [stored 0.114829 ft]; FREON_OUT_R3=0.00°; F_Mid_STR6=795 mm  [stored 2.60827 ft]; F_OffSet=255 mm  [stored 0.836614 ft]; Frequency (Hz)=50; Is_STR5=Sì; Is_STR6=No; Lw (dBA)=83; Maximum current (A)=183.2; Nominal current (A)=102.9; PF_EN14511_W35W7 (kW)=292.9; PF_EN14511_tC50W7 (kW)=0; PR_EN14511_W45 (kW)=0; PT_EN14511_W7W45 (kW)=339.5; Psm_EN14511_W35W7 (kW)=355.8; QTc (m3/h)=58.3; Qc (m3/h)=61.2; Qe (m3/h)=50.4; Qr (m3/h)=0; REC_IN_A=200 mm  [stored 0.656168 ft]; REC_IN_B=250 mm  [stored 0.82021 ft]; REC_IN_C=250 mm  [stored 0.82021 ft]; REC_IN_R3=0.00°; REC_OUT_A=200 mm  [stored 0.656168 ft]; REC_OUT_B=300 mm  [stored 0.984252 ft]; REC_OUT_C=250 mm  [stored 0.82021 ft]; REC_OUT_R3=0.00°; RispettoD3=2209 mm  [stored 7.24738 ft]; SCOP_EN14825=6.62; SEER_EN14825=6.34; Starting current (A)=347.4; Type=HEAT PUMP; Voltage (V)=400; Weight (kg)=1505; dPTc (kPa)=60; dPc (kPa)=66; dPe (kPa)=45; dPr (kPa)=0; n. poles=3+N
- THHETU 4350: COND_IN_A=2209 mm  [stored 7.24738 ft]; COND_IN_B=1290 mm  [stored 4.23228 ft]; COND_IN_C=220 mm  [stored 0.721785 ft]; COND_IN_R3=269.98°; COND_OUT_A=2209 mm  [stored 7.24738 ft]; COND_OUT_B=1680 mm  [stored 5.51181 ft]; COND_OUT_C=220 mm  [stored 0.721785 ft]; COND_OUT_R3=269.98°; COP_EN14511_W7W45=4.04; DS_IN_A=2209 mm  [stored 7.24738 ft]; DS_IN_B=475 mm  [stored 1.5584 ft]; DS_IN_C=204 mm  [stored 0.669291 ft]; DS_IN_R3=269.98°; DS_OUT_A=2209 mm  [stored 7.24738 ft]; DS_OUT_B=725 mm  [stored 2.37861 ft]; DS_OUT_C=204 mm  [stored 0.669291 ft]; DS_OUT_R3=269.98°; EER_EN14511_W35W7=4.36; EER_EN14511_tC50W7=0; EVAP_IN_A=2209 mm  [stored 7.24738 ft]; EVAP_IN_R3=269.98°; EVAP_OUT_A=2209 mm  [stored 7.24738 ft]; EVAP_OUT_R3=269.98°; FREON_IN_A=200 mm  [stored 0.656168 ft]; FREON_IN_B=300 mm  [stored 0.984252 ft]; FREON_IN_C=150 mm  [stored 0.492126 ft]; FREON_IN_Diametro=22 mm  [stored 0.0721785 ft]; FREON_IN_R3=0.00°; FREON_OUT_A=200 mm  [stored 0.656168 ft]; FREON_OUT_B=300 mm  [stored 0.984252 ft]; FREON_OUT_C=200 mm  [stored 0.656168 ft]; FREON_OUT_Diametro=35 mm  [stored 0.114829 ft]; FREON_OUT_R3=0.00°; F_Mid_STR6=795 mm  [stored 2.60827 ft]; F_OffSet=255 mm  [stored 0.836614 ft]; Frequency (Hz)=50; Is_STR5=Sì; Is_STR6=No; Lw (dBA)=84; Maximum current (A)=216.4; Nominal current (A)=128.3; PF_EN14511_W35W7 (kW)=337.8; PF_EN14511_tC50W7 (kW)=0; PR_EN14511_W45 (kW)=0; PT_EN14511_W7W45 (kW)=393.8; Psm_EN14511_W35W7 (kW)=410.3; QTc (m3/h)=67.6; Qc (m3/h)=70.6; Qe (m3/h)=58.2; Qr (m3/h)=0; REC_IN_A=200 mm  [stored 0.656168 ft]; REC_IN_B=250 mm  [stored 0.82021 ft]; REC_IN_C=250 mm  [stored 0.82021 ft]; REC_IN_R3=0.00°; REC_OUT_A=200 mm  [stored 0.656168 ft]; REC_OUT_B=300 mm  [stored 0.984252 ft]; REC_OUT_C=250 mm  [stored 0.82021 ft]; REC_OUT_R3=0.00°; RispettoD3=2209 mm  [stored 7.24738 ft]; SCOP_EN14825=6.62; SEER_EN14825=6.32; Starting current (A)=480; Type=HEAT PUMP; Voltage (V)=400; Weight (kg)=1565; dPTc (kPa)=57; dPc (kPa)=62; dPe (kPa)=42; dPr (kPa)=0; n. poles=3+N
- THHETU 4395: COND_IN_A=2209 mm  [stored 7.24738 ft]; COND_IN_B=1290 mm  [stored 4.23228 ft]; COND_IN_C=220 mm  [stored 0.721785 ft]; COND_IN_R3=269.98°; COND_OUT_A=2209 mm  [stored 7.24738 ft]; COND_OUT_B=1680 mm  [stored 5.51181 ft]; COND_OUT_C=220 mm  [stored 0.721785 ft]; COND_OUT_R3=269.98°; COP_EN14511_W7W45=3.95; DS_IN_A=2209 mm  [stored 7.24738 ft]; DS_IN_B=475 mm  [stored 1.5584 ft]; DS_IN_C=204 mm  [stored 0.669291 ft]; DS_IN_R3=269.98°; DS_OUT_A=2209 mm  [stored 7.24738 ft]; DS_OUT_B=725 mm  [stored 2.37861 ft]; DS_OUT_C=204 mm  [stored 0.669291 ft]; DS_OUT_R3=269.98°; EER_EN14511_W35W7=4.26; EER_EN14511_tC50W7=0; EVAP_IN_A=2209 mm  [stored 7.24738 ft]; EVAP_IN_R3=269.98°; EVAP_OUT_A=2209 mm  [stored 7.24738 ft]; EVAP_OUT_R3=269.98°; FREON_IN_A=200 mm  [stored 0.656168 ft]; FREON_IN_B=300 mm  [stored 0.984252 ft]; FREON_IN_C=150 mm  [stored 0.492126 ft]; FREON_IN_Diametro=22 mm  [stored 0.0721785 ft]; FREON_IN_R3=0.00°; FREON_OUT_A=200 mm  [stored 0.656168 ft]; FREON_OUT_B=300 mm  [stored 0.984252 ft]; FREON_OUT_C=200 mm  [stored 0.656168 ft]; FREON_OUT_Diametro=35 mm  [stored 0.114829 ft]; FREON_OUT_R3=0.00°; F_Mid_STR6=795 mm  [stored 2.60827 ft]; F_OffSet=255 mm  [stored 0.836614 ft]; Frequency (Hz)=50; Is_STR5=Sì; Is_STR6=No; Lw (dBA)=85; Maximum current (A)=249.6; Nominal current (A)=155.2; PF_EN14511_W35W7 (kW)=380.3; PF_EN14511_tC50W7 (kW)=0; PR_EN14511_W45 (kW)=0; PT_EN14511_W7W45 (kW)=444.3; Psm_EN14511_W35W7 (kW)=463.3; QTc (m3/h)=76.3; Qc (m3/h)=79.7; Qe (m3/h)=65.5; Qr (m3/h)=0; REC_IN_A=200 mm  [stored 0.656168 ft]; REC_IN_B=250 mm  [stored 0.82021 ft]; REC_IN_C=250 mm  [stored 0.82021 ft]; REC_IN_R3=0.00°; REC_OUT_A=200 mm  [stored 0.656168 ft]; REC_OUT_B=300 mm  [stored 0.984252 ft]; REC_OUT_C=250 mm  [stored 0.82021 ft]; REC_OUT_R3=0.00°; RispettoD3=2209 mm  [stored 7.24738 ft]; SCOP_EN14825=6.58; SEER_EN14825=6.39; Starting current (A)=513.2; Type=HEAT PUMP; Voltage (V)=400; Weight (kg)=1585; dPTc (kPa)=71; dPc (kPa)=77; dPe (kPa)=52; dPr (kPa)=0; n. poles=3+N
- TXHETU 4185: COND_IN_A=2209 mm  [stored 7.24738 ft]; COND_IN_B=1290 mm  [stored 4.23228 ft]; COND_IN_C=220 mm  [stored 0.721785 ft]; COND_IN_R3=269.98°; COND_OUT_A=2209 mm  [stored 7.24738 ft]; COND_OUT_B=1680 mm  [stored 5.51181 ft]; COND_OUT_C=220 mm  [stored 0.721785 ft]; COND_OUT_R3=269.98°; COP_EN14511_W7W45=4.02; DS_IN_A=200 mm  [stored 0.656168 ft]; DS_IN_B=250 mm  [stored 0.82021 ft]; DS_IN_C=150 mm  [stored 0.492126 ft]; DS_IN_R3=0.00°; DS_OUT_A=200 mm  [stored 0.656168 ft]; DS_OUT_B=250 mm  [stored 0.82021 ft]; DS_OUT_C=200 mm  [stored 0.656168 ft]; DS_OUT_R3=0.00°; EER_EN14511_W35W7=4.47; EER_EN14511_tC50W7=0; EVAP_IN_A=2209 mm  [stored 7.24738 ft]; EVAP_IN_R3=269.98°; EVAP_OUT_A=2209 mm  [stored 7.24738 ft]; EVAP_OUT_R3=269.98°; FREON_IN_A=200 mm  [stored 0.656168 ft]; FREON_IN_B=300 mm  [stored 0.984252 ft]; FREON_IN_C=150 mm  [stored 0.492126 ft]; FREON_IN_Diametro=22 mm  [stored 0.0721785 ft]; FREON_IN_R3=0.00°; FREON_OUT_A=200 mm  [stored 0.656168 ft]; FREON_OUT_B=300 mm  [stored 0.984252 ft]; FREON_OUT_C=200 mm  [stored 0.656168 ft]; FREON_OUT_Diametro=35 mm  [stored 0.114829 ft]; FREON_OUT_R3=0.00°; F_Mid_STR6=795 mm  [stored 2.60827 ft]; F_OffSet=255 mm  [stored 0.836614 ft]; Frequency (Hz)=50; Is_STR5=Sì; Is_STR6=No; Lw (dBA)=79; Maximum current (A)=117.16; Nominal current (A)=77.8; PF_EN14511_W35W7 (kW)=180; PF_EN14511_tC50W7 (kW)=0; PR_EN14511_W45 (kW)=202.4; PT_EN14511_W7W45 (kW)=200.1; Psm_EN14511_W35W7 (kW)=218; QTc (m3/h)=34.4; Qc (m3/h)=37.5; Qe (m3/h)=31; Qr (m3/h)=34.4; REC_IN_A=2209 mm  [stored 7.24738 ft]; REC_IN_B=475 mm  [stored 1.5584 ft]; REC_IN_C=220 mm  [stored 0.721785 ft]; REC_IN_R3=269.98°; REC_OUT_A=2209 mm  [stored 7.24738 ft]; REC_OUT_B=865 mm  [stored 2.83793 ft]; REC_OUT_C=220 mm  [stored 0.721785 ft]; REC_OUT_R3=269.98°; RispettoD3=2209 mm  [stored 7.24738 ft]; SCOP_EN14825=6.79; SEER_EN14825=6.06; Starting current (A)=284.87; Type=HEAT PUMP; Voltage (V)=400; Weight (kg)=1205; dPTc (kPa)=32; dPc (kPa)=38; dPe (kPa)=26; dPr (kPa)=32; n. poles=3+N
- TXHETU 4210: COND_IN_A=2209 mm  [stored 7.24738 ft]; COND_IN_B=1290 mm  [stored 4.23228 ft]; COND_IN_C=220 mm  [stored 0.721785 ft]; COND_IN_R3=269.98°; COND_OUT_A=2209 mm  [stored 7.24738 ft]; COND_OUT_B=1680 mm  [stored 5.51181 ft]; COND_OUT_C=220 mm  [stored 0.721785 ft]; COND_OUT_R3=269.98°; COP_EN14511_W7W45=3.91; DS_IN_A=200 mm  [stored 0.656168 ft]; DS_IN_B=250 mm  [stored 0.82021 ft]; DS_IN_C=150 mm  [stored 0.492126 ft]; DS_IN_R3=0.00°; DS_OUT_A=200 mm  [stored 0.656168 ft]; DS_OUT_B=250 mm  [stored 0.82021 ft]; DS_OUT_C=200 mm  [stored 0.656168 ft]; DS_OUT_R3=0.00°; EER_EN14511_W35W7=4.28; EER_EN14511_tC50W7=0; EVAP_IN_A=2209 mm  [stored 7.24738 ft]; EVAP_IN_R3=269.98°; EVAP_OUT_A=2209 mm  [stored 7.24738 ft]; EVAP_OUT_R3=269.98°; FREON_IN_A=200 mm  [stored 0.656168 ft]; FREON_IN_B=300 mm  [stored 0.984252 ft]; FREON_IN_C=150 mm  [stored 0.492126 ft]; FREON_IN_Diametro=22 mm  [stored 0.0721785 ft]; FREON_IN_R3=0.00°; FREON_OUT_A=200 mm  [stored 0.656168 ft]; FREON_OUT_B=300 mm  [stored 0.984252 ft]; FREON_OUT_C=200 mm  [stored 0.656168 ft]; FREON_OUT_Diametro=35 mm  [stored 0.114829 ft]; FREON_OUT_R3=0.00°; F_Mid_STR6=795 mm  [stored 2.60827 ft]; F_OffSet=255 mm  [stored 0.836614 ft]; Frequency (Hz)=50; Is_STR5=Sì; Is_STR6=No; Lw (dBA)=79; Maximum current (A)=135.9; Nominal current (A)=88.7; PF_EN14511_W35W7 (kW)=206.7; PF_EN14511_tC50W7 (kW)=0; PR_EN14511_W45 (kW)=236.9; PT_EN14511_W7W45 (kW)=234.6; Psm_EN14511_W35W7 (kW)=252.1; QTc (m3/h)=40.3; Qc (m3/h)=43.4; Qe (m3/h)=35.6; Qr (m3/h)=40.3; REC_IN_A=2209 mm  [stored 7.24738 ft]; REC_IN_B=475 mm  [stored 1.5584 ft]; REC_IN_C=220 mm  [stored 0.721785 ft]; REC_IN_R3=269.98°; REC_OUT_A=2209 mm  [stored 7.24738 ft]; REC_OUT_B=865 mm  [stored 2.83793 ft]; REC_OUT_C=220 mm  [stored 0.721785 ft]; REC_OUT_R3=269.98°; RispettoD3=2209 mm  [stored 7.24738 ft]; SCOP_EN14825=6.66; SEER_EN14825=6.04; Starting current (A)=324.24; Type=HEAT PUMP; Voltage (V)=400; Weight (kg)=1315; dPTc (kPa)=42; dPc (kPa)=49; dPe (kPa)=33; dPr (kPa)=42; n. poles=3+N
- TXHETU 4240: COND_IN_A=2209 mm  [stored 7.24738 ft]; COND_IN_B=1290 mm  [stored 4.23228 ft]; COND_IN_C=220 mm  [stored 0.721785 ft]; COND_IN_R3=269.98°; COND_OUT_A=2209 mm  [stored 7.24738 ft]; COND_OUT_B=1680 mm  [stored 5.51181 ft]; COND_OUT_C=220 mm  [stored 0.721785 ft]; COND_OUT_R3=269.98°; COP_EN14511_W7W45=3.88; DS_IN_A=200 mm  [stored 0.656168 ft]; DS_IN_B=250 mm  [stored 0.82021 ft]; DS_IN_C=150 mm  [stored 0.492126 ft]; DS_IN_R3=0.00°; DS_OUT_A=200 mm  [stored 0.656168 ft]; DS_OUT_B=250 mm  [stored 0.82021 ft]; DS_OUT_C=200 mm  [stored 0.656168 ft]; DS_OUT_R3=0.00°; EER_EN14511_W35W7=4.21; EER_EN14511_tC50W7=0; EVAP_IN_A=2209 mm  [stored 7.24738 ft]; EVAP_IN_R3=269.98°; EVAP_OUT_A=2209 mm  [stored 7.24738 ft]; EVAP_OUT_R3=269.98°; FREON_IN_A=200 mm  [stored 0.656168 ft]; FREON_IN_B=300 mm  [stored 0.984252 ft]; FREON_IN_C=150 mm  [stored 0.492126 ft]; FREON_IN_Diametro=22 mm  [stored 0.0721785 ft]; FREON_IN_R3=0.00°; FREON_OUT_A=200 mm  [stored 0.656168 ft]; FREON_OUT_B=300 mm  [stored 0.984252 ft]; FREON_OUT_C=200 mm  [stored 0.656168 ft]; FREON_OUT_Diametro=35 mm  [stored 0.114829 ft]; FREON_OUT_R3=0.00°; F_Mid_STR6=795 mm  [stored 2.60827 ft]; F_OffSet=255 mm  [stored 0.836614 ft]; Frequency (Hz)=50; Is_STR5=Sì; Is_STR6=No; Lw (dBA)=80; Maximum current (A)=154.64; Nominal current (A)=98.3; PF_EN14511_W35W7 (kW)=232.4; PF_EN14511_tC50W7 (kW)=0; PR_EN14511_W45 (kW)=270.2; PT_EN14511_W7W45 (kW)=267.2; Psm_EN14511_W35W7 (kW)=284.5; QTc (m3/h)=45.9; Qc (m3/h)=48.9; Qe (m3/h)=40; Qr (m3/h)=45.9; REC_IN_A=2209 mm  [stored 7.24738 ft]; REC_IN_B=475 mm  [stored 1.5584 ft]; REC_IN_C=220 mm  [stored 0.721785 ft]; REC_IN_R3=269.98°; REC_OUT_A=2209 mm  [stored 7.24738 ft]; REC_OUT_B=865 mm  [stored 2.83793 ft]; REC_OUT_C=220 mm  [stored 0.721785 ft]; REC_OUT_R3=269.98°; RispettoD3=2209 mm  [stored 7.24738 ft]; SCOP_EN14825=6.54; SEER_EN14825=6.19; Starting current (A)=342.98; Type=HEAT PUMP; Voltage (V)=400; Weight (kg)=1455; dPTc (kPa)=38; dPc (kPa)=43; dPe (kPa)=29; dPr (kPa)=38; n. poles=3+N
- TXHETU 4275: COND_IN_A=2209 mm  [stored 7.24738 ft]; COND_IN_B=1290 mm  [stored 4.23228 ft]; COND_IN_C=220 mm  [stored 0.721785 ft]; COND_IN_R3=269.98°; COND_OUT_A=2209 mm  [stored 7.24738 ft]; COND_OUT_B=1680 mm  [stored 5.51181 ft]; COND_OUT_C=220 mm  [stored 0.721785 ft]; COND_OUT_R3=269.98°; COP_EN14511_W7W45=3.93; DS_IN_A=200 mm  [stored 0.656168 ft]; DS_IN_B=250 mm  [stored 0.82021 ft]; DS_IN_C=150 mm  [stored 0.492126 ft]; DS_IN_R3=0.00°; DS_OUT_A=200 mm  [stored 0.656168 ft]; DS_OUT_B=250 mm  [stored 0.82021 ft]; DS_OUT_C=200 mm  [stored 0.656168 ft]; DS_OUT_R3=0.00°; EER_EN14511_W35W7=4.24; EER_EN14511_tC50W7=0; EVAP_IN_A=2209 mm  [stored 7.24738 ft]; EVAP_IN_R3=269.98°; EVAP_OUT_A=2209 mm  [stored 7.24738 ft]; EVAP_OUT_R3=269.98°; FREON_IN_A=200 mm  [stored 0.656168 ft]; FREON_IN_B=300 mm  [stored 0.984252 ft]; FREON_IN_C=150 mm  [stored 0.492126 ft]; FREON_IN_Diametro=22 mm  [stored 0.0721785 ft]; FREON_IN_R3=0.00°; FREON_OUT_A=200 mm  [stored 0.656168 ft]; FREON_OUT_B=300 mm  [stored 0.984252 ft]; FREON_OUT_C=200 mm  [stored 0.656168 ft]; FREON_OUT_Diametro=35 mm  [stored 0.114829 ft]; FREON_OUT_R3=0.00°; F_Mid_STR6=795 mm  [stored 2.60827 ft]; F_OffSet=255 mm  [stored 0.836614 ft]; Frequency (Hz)=50; Is_STR5=Sì; Is_STR6=No; Lw (dBA)=81; Maximum current (A)=169.9; Nominal current (A)=108.7; PF_EN14511_W35W7 (kW)=259.3; PF_EN14511_tC50W7 (kW)=0; PR_EN14511_W45 (kW)=301.8; PT_EN14511_W7W45 (kW)=299; Psm_EN14511_W35W7 (kW)=316.7; QTc (m3/h)=51.4; Qc (m3/h)=54.5; Qe (m3/h)=44.7; Qr (m3/h)=51.4; REC_IN_A=2209 mm  [stored 7.24738 ft]; REC_IN_B=475 mm  [stored 1.5584 ft]; REC_IN_C=220 mm  [stored 0.721785 ft]; REC_IN_R3=269.98°; REC_OUT_A=2209 mm  [stored 7.24738 ft]; REC_OUT_B=865 mm  [stored 2.83793 ft]; REC_OUT_C=220 mm  [stored 0.721785 ft]; REC_OUT_R3=269.98°; RispettoD3=2209 mm  [stored 7.24738 ft]; SCOP_EN14825=6.47; SEER_EN14825=6.22; Starting current (A)=383.61; Type=HEAT PUMP; Voltage (V)=400; Weight (kg)=1500; dPTc (kPa)=46; dPc (kPa)=52; dPe (kPa)=35; dPr (kPa)=46; n. poles=3+N
- TXHETU 4305: COND_IN_A=2209 mm  [stored 7.24738 ft]; COND_IN_B=1290 mm  [stored 4.23228 ft]; COND_IN_C=220 mm  [stored 0.721785 ft]; COND_IN_R3=269.98°; COND_OUT_A=2209 mm  [stored 7.24738 ft]; COND_OUT_B=1680 mm  [stored 5.51181 ft]; COND_OUT_C=220 mm  [stored 0.721785 ft]; COND_OUT_R3=269.98°; COP_EN14511_W7W45=3.96; DS_IN_A=200 mm  [stored 0.656168 ft]; DS_IN_B=250 mm  [stored 0.82021 ft]; DS_IN_C=150 mm  [stored 0.492126 ft]; DS_IN_R3=0.00°; DS_OUT_A=200 mm  [stored 0.656168 ft]; DS_OUT_B=250 mm  [stored 0.82021 ft]; DS_OUT_C=200 mm  [stored 0.656168 ft]; DS_OUT_R3=0.00°; EER_EN14511_W35W7=4.26; EER_EN14511_tC50W7=0; EVAP_IN_A=2209 mm  [stored 7.24738 ft]; EVAP_IN_R3=269.98°; EVAP_OUT_A=2209 mm  [stored 7.24738 ft]; EVAP_OUT_R3=269.98°; FREON_IN_A=200 mm  [stored 0.656168 ft]; FREON_IN_B=300 mm  [stored 0.984252 ft]; FREON_IN_C=150 mm  [stored 0.492126 ft]; FREON_IN_Diametro=22 mm  [stored 0.0721785 ft]; FREON_IN_R3=0.00°; FREON_OUT_A=200 mm  [stored 0.656168 ft]; FREON_OUT_B=300 mm  [stored 0.984252 ft]; FREON_OUT_C=200 mm  [stored 0.656168 ft]; FREON_OUT_Diametro=35 mm  [stored 0.114829 ft]; FREON_OUT_R3=0.00°; F_Mid_STR6=795 mm  [stored 2.60827 ft]; F_OffSet=255 mm  [stored 0.836614 ft]; Frequency (Hz)=50; Is_STR5=Sì; Is_STR6=No; Lw (dBA)=83; Maximum current (A)=185.16; Nominal current (A)=119.1; PF_EN14511_W35W7 (kW)=286.4; PF_EN14511_tC50W7 (kW)=0; PR_EN14511_W45 (kW)=335.1; PT_EN14511_W7W45 (kW)=332.3; Psm_EN14511_W35W7 (kW)=349.3; QTc (m3/h)=57.1; Qc (m3/h)=60.1; Qe (m3/h)=49.3; Qr (m3/h)=57.1; REC_IN_A=2209 mm  [stored 7.24738 ft]; REC_IN_B=475 mm  [stored 1.5584 ft]; REC_IN_C=220 mm  [stored 0.721785 ft]; REC_IN_R3=269.98°; REC_OUT_A=2209 mm  [stored 7.24738 ft]; REC_OUT_B=865 mm  [stored 2.83793 ft]; REC_OUT_C=220 mm  [stored 0.721785 ft]; REC_OUT_R3=269.98°; RispettoD3=2209 mm  [stored 7.24738 ft]; SCOP_EN14825=6.48; SEER_EN14825=6.29; Starting current (A)=398.87; Type=HEAT PUMP; Voltage (V)=400; Weight (kg)=1520; dPTc (kPa)=58; dPc (kPa)=64; dPe (kPa)=43; dPr (kPa)=58; n. poles=3+N
- TXHETU 4350: COND_IN_A=2209 mm  [stored 7.24738 ft]; COND_IN_B=1290 mm  [stored 4.23228 ft]; COND_IN_C=220 mm  [stored 0.721785 ft]; COND_IN_R3=269.98°; COND_OUT_A=2209 mm  [stored 7.24738 ft]; COND_OUT_B=1680 mm  [stored 5.51181 ft]; COND_OUT_C=220 mm  [stored 0.721785 ft]; COND_OUT_R3=269.98°; COP_EN14511_W7W45=4.01; DS_IN_A=200 mm  [stored 0.656168 ft]; DS_IN_B=250 mm  [stored 0.82021 ft]; DS_IN_C=150 mm  [stored 0.492126 ft]; DS_IN_R3=0.00°; DS_OUT_A=200 mm  [stored 0.656168 ft]; DS_OUT_B=250 mm  [stored 0.82021 ft]; DS_OUT_C=200 mm  [stored 0.656168 ft]; DS_OUT_R3=0.00°; EER_EN14511_W35W7=4.26; EER_EN14511_tC50W7=0; EVAP_IN_A=2209 mm  [stored 7.24738 ft]; EVAP_IN_R3=269.98°; EVAP_OUT_A=2209 mm  [stored 7.24738 ft]; EVAP_OUT_R3=269.98°; FREON_IN_A=200 mm  [stored 0.656168 ft]; FREON_IN_B=300 mm  [stored 0.984252 ft]; FREON_IN_C=150 mm  [stored 0.492126 ft]; FREON_IN_Diametro=22 mm  [stored 0.0721785 ft]; FREON_IN_R3=0.00°; FREON_OUT_A=200 mm  [stored 0.656168 ft]; FREON_OUT_B=300 mm  [stored 0.984252 ft]; FREON_OUT_C=200 mm  [stored 0.656168 ft]; FREON_OUT_Diametro=35 mm  [stored 0.114829 ft]; FREON_OUT_R3=0.00°; F_Mid_STR6=795 mm  [stored 2.60827 ft]; F_OffSet=255 mm  [stored 0.836614 ft]; Frequency (Hz)=50; Is_STR5=Sì; Is_STR6=No; Lw (dBA)=84; Maximum current (A)=207.54; Nominal current (A)=130; PF_EN14511_W35W7 (kW)=324.8; PF_EN14511_tC50W7 (kW)=0; PR_EN14511_W45 (kW)=384.2; PT_EN14511_W7W45 (kW)=380.2; Psm_EN14511_W35W7 (kW)=396.3; QTc (m3/h)=65.3; Qc (m3/h)=68.2; Qe (m3/h)=55.9; Qr (m3/h)=65.3; REC_IN_A=2209 mm  [stored 7.24738 ft]; REC_IN_B=475 mm  [stored 1.5584 ft]; REC_IN_C=220 mm  [stored 0.721785 ft]; REC_IN_R3=269.98°; REC_OUT_A=2209 mm  [stored 7.24738 ft]; REC_OUT_B=865 mm  [stored 2.83793 ft]; REC_OUT_C=220 mm  [stored 0.721785 ft]; REC_OUT_R3=269.98°; RispettoD3=2209 mm  [stored 7.24738 ft]; SCOP_EN14825=6.49; SEER_EN14825=6.29; Starting current (A)=444.06; Type=HEAT PUMP; Voltage (V)=400; Weight (kg)=1675; dPTc (kPa)=53; dPc (kPa)=58; dPe (kPa)=39; dPr (kPa)=53; n. poles=3+N
- TXHETU 4395: COND_IN_A=2209 mm  [stored 7.24738 ft]; COND_IN_B=1290 mm  [stored 4.23228 ft]; COND_IN_C=220 mm  [stored 0.721785 ft]; COND_IN_R3=269.98°; COND_OUT_A=2209 mm  [stored 7.24738 ft]; COND_OUT_B=1680 mm  [stored 5.51181 ft]; COND_OUT_C=220 mm  [stored 0.721785 ft]; COND_OUT_R3=269.98°; COP_EN14511_W7W45=3.92; DS_IN_A=200 mm  [stored 0.656168 ft]; DS_IN_B=250 mm  [stored 0.82021 ft]; DS_IN_C=150 mm  [stored 0.492126 ft]; DS_IN_R3=0.00°; DS_OUT_A=200 mm  [stored 0.656168 ft]; DS_OUT_B=250 mm  [stored 0.82021 ft]; DS_OUT_C=200 mm  [stored 0.656168 ft]; DS_OUT_R3=0.00°; EER_EN14511_W35W7=4.22; EER_EN14511_tC50W7=0; EVAP_IN_A=2209 mm  [stored 7.24738 ft]; EVAP_IN_R3=269.98°; EVAP_OUT_A=2209 mm  [stored 7.24738 ft]; EVAP_OUT_R3=269.98°; FREON_IN_A=200 mm  [stored 0.656168 ft]; FREON_IN_B=300 mm  [stored 0.984252 ft]; FREON_IN_C=150 mm  [stored 0.492126 ft]; FREON_IN_Diametro=22 mm  [stored 0.0721785 ft]; FREON_IN_R3=0.00°; FREON_OUT_A=200 mm  [stored 0.656168 ft]; FREON_OUT_B=300 mm  [stored 0.984252 ft]; FREON_OUT_C=200 mm  [stored 0.656168 ft]; FREON_OUT_Diametro=35 mm  [stored 0.114829 ft]; FREON_OUT_R3=0.00°; F_Mid_STR6=795 mm  [stored 2.60827 ft]; F_OffSet=255 mm  [stored 0.836614 ft]; Frequency (Hz)=50; Is_STR5=Sì; Is_STR6=No; Lw (dBA)=85; Maximum current (A)=229.92; Nominal current (A)=141.7; PF_EN14511_W35W7 (kW)=365.2; PF_EN14511_tC50W7 (kW)=0; PR_EN14511_W45 (kW)=428.3; PT_EN14511_W7W45 (kW)=424.8; Psm_EN14511_W35W7 (kW)=445.7; QTc (m3/h)=73; Qc (m3/h)=76.7; Qe (m3/h)=62.9; Qr (m3/h)=73; REC_IN_A=2209 mm  [stored 7.24738 ft]; REC_IN_B=475 mm  [stored 1.5584 ft]; REC_IN_C=220 mm  [stored 0.721785 ft]; REC_IN_R3=269.98°; REC_OUT_A=2209 mm  [stored 7.24738 ft]; REC_OUT_B=865 mm  [stored 2.83793 ft]; REC_OUT_C=220 mm  [stored 0.721785 ft]; REC_OUT_R3=269.98°; RispettoD3=2209 mm  [stored 7.24738 ft]; SCOP_EN14825=6.47; SEER_EN14825=6.3; Starting current (A)=466.44; Type=HEAT PUMP; Voltage (V)=400; Weight (kg)=1770; dPTc (kPa)=66; dPc (kPa)=73; dPe (kPa)=49; dPr (kPa)=66; n. poles=3+N
- TCEETU 4185: COND_IN_A=200 mm  [stored 0.656168 ft]; COND_IN_B=350 mm  [stored 1.14829 ft]; COND_IN_C=150 mm  [stored 0.492126 ft]; COND_IN_R3=0.00°; COND_OUT_A=200 mm  [stored 0.656168 ft]; COND_OUT_B=350 mm  [stored 1.14829 ft]; COND_OUT_C=200 mm  [stored 0.656168 ft]; COND_OUT_R3=0.00°; COP_EN14511_W7W45=0; DS_IN_A=2209 mm  [stored 7.24738 ft]; DS_IN_B=475 mm  [stored 1.5584 ft]; DS_IN_C=204 mm  [stored 0.669291 ft]; DS_IN_R3=269.98°; DS_OUT_A=2209 mm  [stored 7.24738 ft]; DS_OUT_B=725 mm  [stored 2.37861 ft]; DS_OUT_C=204 mm  [stored 0.669291 ft]; DS_OUT_R3=269.98°; EER_EN14511_W35W7=0; EER_EN14511_tC50W7=3.51; EVAP_IN_A=2209 mm  [stored 7.24738 ft]; EVAP_IN_R3=269.98°; EVAP_OUT_A=2209 mm  [stored 7.24738 ft]; EVAP_OUT_R3=269.98°; FREON_IN_A=2209 mm  [stored 7.24738 ft]; FREON_IN_B=1290 mm  [stored 4.23228 ft]; FREON_IN_C=220 mm  [stored 0.721785 ft]; FREON_IN_Diametro=22 mm  [stored 0.0721785 ft]; FREON_IN_R3=269.98°; FREON_OUT_A=2209 mm  [stored 7.24738 ft]; FREON_OUT_B=1680 mm  [stored 5.51181 ft]; FREON_OUT_C=220 mm  [stored 0.721785 ft]; FREON_OUT_Diametro=35 mm  [stored 0.114829 ft]; FREON_OUT_R3=269.98°; F_Mid_STR6=795 mm  [stored 2.60827 ft]; F_OffSet=255 mm  [stored 0.836614 ft]; Frequency (Hz)=50; Is_STR5=Sì; Is_STR6=No; Lw (dBA)=79; Maximum current (A)=108; Nominal current (A)=84.6; PF_EN14511_W35W7 (kW)=0; PF_EN14511_tC50W7 (kW)=166.5; PR_EN14511_W45 (kW)=0; PT_EN14511_W7W45 (kW)=0; Psm_EN14511_W35W7 (kW)=0; QTc (m3/h)=0; Qc (m3/h)=0; Qe (m3/h)=28.7; Qr (m3/h)=0; REC_IN_A=2209 mm  [stored 7.24738 ft]; REC_IN_B=475 mm  [stored 1.5584 ft]; REC_IN_C=220 mm  [stored 0.721785 ft]; REC_IN_R3=269.98°; REC_OUT_A=2209 mm  [stored 7.24738 ft]; REC_OUT_B=865 mm  [stored 2.83793 ft]; REC_OUT_C=220 mm  [stored 0.721785 ft]; REC_OUT_R3=269.98°; RispettoD3=2209 mm  [stored 7.24738 ft]; SCOP_EN14825=0; SEER_EN14825=0; Starting current (A)=253; Type=CHILLER; Voltage (V)=400; Weight (kg)=1040; dPTc (kPa)=0; dPc (kPa)=0; dPe (kPa)=22; dPr (kPa)=0; n. poles=3+N
- TCEETU 4210: COND_IN_A=200 mm  [stored 0.656168 ft]; COND_IN_B=350 mm  [stored 1.14829 ft]; COND_IN_C=150 mm  [stored 0.492126 ft]; COND_IN_R3=0.00°; COND_OUT_A=200 mm  [stored 0.656168 ft]; COND_OUT_B=350 mm  [stored 1.14829 ft]; COND_OUT_C=200 mm  [stored 0.656168 ft]; COND_OUT_R3=0.00°; COP_EN14511_W7W45=0; DS_IN_A=2209 mm  [stored 7.24738 ft]; DS_IN_B=475 mm  [stored 1.5584 ft]; DS_IN_C=204 mm  [stored 0.669291 ft]; DS_IN_R3=269.98°; DS_OUT_A=2209 mm  [stored 7.24738 ft]; DS_OUT_B=725 mm  [stored 2.37861 ft]; DS_OUT_C=204 mm  [stored 0.669291 ft]; DS_OUT_R3=269.98°; EER_EN14511_W35W7=0; EER_EN14511_tC50W7=3.45; EVAP_IN_A=2209 mm  [stored 7.24738 ft]; EVAP_IN_R3=269.98°; EVAP_OUT_A=2209 mm  [stored 7.24738 ft]; EVAP_OUT_R3=269.98°; FREON_IN_A=2209 mm  [stored 7.24738 ft]; FREON_IN_B=1290 mm  [stored 4.23228 ft]; FREON_IN_C=220 mm  [stored 0.721785 ft]; FREON_IN_Diametro=22 mm  [stored 0.0721785 ft]; FREON_IN_R3=269.98°; FREON_OUT_A=2209 mm  [stored 7.24738 ft]; FREON_OUT_B=1680 mm  [stored 5.51181 ft]; FREON_OUT_C=220 mm  [stored 0.721785 ft]; FREON_OUT_Diametro=35 mm  [stored 0.114829 ft]; FREON_OUT_R3=269.98°; F_Mid_STR6=795 mm  [stored 2.60827 ft]; F_OffSet=255 mm  [stored 0.836614 ft]; Frequency (Hz)=50; Is_STR5=Sì; Is_STR6=No; Lw (dBA)=79; Maximum current (A)=128.8; Nominal current (A)=102.1; PF_EN14511_W35W7 (kW)=0; PF_EN14511_tC50W7 (kW)=191; PR_EN14511_W45 (kW)=0; PT_EN14511_W7W45 (kW)=0; Psm_EN14511_W35W7 (kW)=0; QTc (m3/h)=0; Qc (m3/h)=0; Qe (m3/h)=32.9; Qr (m3/h)=0; REC_IN_A=2209 mm  [stored 7.24738 ft]; REC_IN_B=475 mm  [stored 1.5584 ft]; REC_IN_C=220 mm  [stored 0.721785 ft]; REC_IN_R3=269.98°; REC_OUT_A=2209 mm  [stored 7.24738 ft]; REC_OUT_B=865 mm  [stored 2.83793 ft]; REC_OUT_C=220 mm  [stored 0.721785 ft]; REC_OUT_R3=269.98°; RispettoD3=2209 mm  [stored 7.24738 ft]; SCOP_EN14825=0; SEER_EN14825=0; Starting current (A)=302.4; Type=CHILLER; Voltage (V)=400; Weight (kg)=1050; dPTc (kPa)=0; dPc (kPa)=0; dPe (kPa)=28; dPr (kPa)=0; n. poles=3+N
- TCEETU 4240: COND_IN_A=200 mm  [stored 0.656168 ft]; COND_IN_B=350 mm  [stored 1.14829 ft]; COND_IN_C=150 mm  [stored 0.492126 ft]; COND_IN_R3=0.00°; COND_OUT_A=200 mm  [stored 0.656168 ft]; COND_OUT_B=350 mm  [stored 1.14829 ft]; COND_OUT_C=200 mm  [stored 0.656168 ft]; COND_OUT_R3=0.00°; COP_EN14511_W7W45=0; DS_IN_A=2209 mm  [stored 7.24738 ft]; DS_IN_B=475 mm  [stored 1.5584 ft]; DS_IN_C=204 mm  [stored 0.669291 ft]; DS_IN_R3=269.98°; DS_OUT_A=2209 mm  [stored 7.24738 ft]; DS_OUT_B=725 mm  [stored 2.37861 ft]; DS_OUT_C=204 mm  [stored 0.669291 ft]; DS_OUT_R3=269.98°; EER_EN14511_W35W7=0; EER_EN14511_tC50W7=3.43; EVAP_IN_A=2209 mm  [stored 7.24738 ft]; EVAP_IN_R3=269.98°; EVAP_OUT_A=2209 mm  [stored 7.24738 ft]; EVAP_OUT_R3=269.98°; FREON_IN_A=2209 mm  [stored 7.24738 ft]; FREON_IN_B=1290 mm  [stored 4.23228 ft]; FREON_IN_C=220 mm  [stored 0.721785 ft]; FREON_IN_Diametro=22 mm  [stored 0.0721785 ft]; FREON_IN_R3=269.98°; FREON_OUT_A=2209 mm  [stored 7.24738 ft]; FREON_OUT_B=1680 mm  [stored 5.51181 ft]; FREON_OUT_C=220 mm  [stored 0.721785 ft]; FREON_OUT_Diametro=35 mm  [stored 0.114829 ft]; FREON_OUT_R3=269.98°; F_Mid_STR6=795 mm  [stored 2.60827 ft]; F_OffSet=255 mm  [stored 0.836614 ft]; Frequency (Hz)=50; Is_STR5=Sì; Is_STR6=No; Lw (dBA)=80; Maximum current (A)=149.6; Nominal current (A)=119.1; PF_EN14511_W35W7 (kW)=0; PF_EN14511_tC50W7 (kW)=215.1; PR_EN14511_W45 (kW)=0; PT_EN14511_W7W45 (kW)=0; Psm_EN14511_W35W7 (kW)=0; QTc (m3/h)=0; Qc (m3/h)=0; Qe (m3/h)=37; Qr (m3/h)=0; REC_IN_A=2209 mm  [stored 7.24738 ft]; REC_IN_B=475 mm  [stored 1.5584 ft]; REC_IN_C=220 mm  [stored 0.721785 ft]; REC_IN_R3=269.98°; REC_OUT_A=2209 mm  [stored 7.24738 ft]; REC_OUT_B=865 mm  [stored 2.83793 ft]; REC_OUT_C=220 mm  [stored 0.721785 ft]; REC_OUT_R3=269.98°; RispettoD3=2209 mm  [stored 7.24738 ft]; SCOP_EN14825=0; SEER_EN14825=0; Starting current (A)=323.2; Type=CHILLER; Voltage (V)=400; Weight (kg)=1070; dPTc (kPa)=0; dPc (kPa)=0; dPe (kPa)=24; dPr (kPa)=0; n. poles=3+N
- TCEETU 4275: COND_IN_A=200 mm  [stored 0.656168 ft]; COND_IN_B=350 mm  [stored 1.14829 ft]; COND_IN_C=150 mm  [stored 0.492126 ft]; COND_IN_R3=0.00°; COND_OUT_A=200 mm  [stored 0.656168 ft]; COND_OUT_B=350 mm  [stored 1.14829 ft]; COND_OUT_C=200 mm  [stored 0.656168 ft]; COND_OUT_R3=0.00°; COP_EN14511_W7W45=0; DS_IN_A=2209 mm  [stored 7.24738 ft]; DS_IN_B=475 mm  [stored 1.5584 ft]; DS_IN_C=204 mm  [stored 0.669291 ft]; DS_IN_R3=269.98°; DS_OUT_A=2209 mm  [stored 7.24738 ft]; DS_OUT_B=725 mm  [stored 2.37861 ft]; DS_OUT_C=204 mm  [stored 0.669291 ft]; DS_OUT_R3=269.98°; EER_EN14511_W35W7=0; EER_EN14511_tC50W7=3.34; EVAP_IN_A=2209 mm  [stored 7.24738 ft]; EVAP_IN_R3=269.98°; EVAP_OUT_A=2209 mm  [stored 7.24738 ft]; EVAP_OUT_R3=269.98°; FREON_IN_A=2209 mm  [stored 7.24738 ft]; FREON_IN_B=1290 mm  [stored 4.23228 ft]; FREON_IN_C=220 mm  [stored 0.721785 ft]; FREON_IN_Diametro=28 mm  [stored 0.0918635 ft]; FREON_IN_R3=269.98°; FREON_OUT_A=2209 mm  [stored 7.24738 ft]; FREON_OUT_B=1680 mm  [stored 5.51181 ft]; FREON_OUT_C=220 mm  [stored 0.721785 ft]; FREON_OUT_Diametro=42 mm  [stored 0.137795 ft]; FREON_OUT_R3=269.98°; F_Mid_STR6=795 mm  [stored 2.60827 ft]; F_OffSet=255 mm  [stored 0.836614 ft]; Frequency (Hz)=50; Is_STR5=Sì; Is_STR6=No; Lw (dBA)=81; Maximum current (A)=166.4; Nominal current (A)=124.6; PF_EN14511_W35W7 (kW)=0; PF_EN14511_tC50W7 (kW)=242.4; PR_EN14511_W45 (kW)=0; PT_EN14511_W7W45 (kW)=0; Psm_EN14511_W35W7 (kW)=0; QTc (m3/h)=0; Qc (m3/h)=0; Qe (m3/h)=41.7; Qr (m3/h)=0; REC_IN_A=2209 mm  [stored 7.24738 ft]; REC_IN_B=475 mm  [stored 1.5584 ft]; REC_IN_C=220 mm  [stored 0.721785 ft]; REC_IN_R3=269.98°; REC_OUT_A=2209 mm  [stored 7.24738 ft]; REC_OUT_B=865 mm  [stored 2.83793 ft]; REC_OUT_C=220 mm  [stored 0.721785 ft]; REC_OUT_R3=269.98°; RispettoD3=2209 mm  [stored 7.24738 ft]; SCOP_EN14825=0; SEER_EN14825=0; Starting current (A)=330.6; Type=CHILLER; Voltage (V)=400; Weight (kg)=1245; dPTc (kPa)=0; dPc (kPa)=0; dPe (kPa)=31; dPr (kPa)=0; n. poles=3+N
- TCEETU 4305: COND_IN_A=200 mm  [stored 0.656168 ft]; COND_IN_B=350 mm  [stored 1.14829 ft]; COND_IN_C=150 mm  [stored 0.492126 ft]; COND_IN_R3=0.00°; COND_OUT_A=200 mm  [stored 0.656168 ft]; COND_OUT_B=350 mm  [stored 1.14829 ft]; COND_OUT_C=200 mm  [stored 0.656168 ft]; COND_OUT_R3=0.00°; COP_EN14511_W7W45=0; DS_IN_A=2209 mm  [stored 7.24738 ft]; DS_IN_B=475 mm  [stored 1.5584 ft]; DS_IN_C=204 mm  [stored 0.669291 ft]; DS_IN_R3=269.98°; DS_OUT_A=2209 mm  [stored 7.24738 ft]; DS_OUT_B=725 mm  [stored 2.37861 ft]; DS_OUT_C=204 mm  [stored 0.669291 ft]; DS_OUT_R3=269.98°; EER_EN14511_W35W7=0; EER_EN14511_tC50W7=3.28; EVAP_IN_A=2209 mm  [stored 7.24738 ft]; EVAP_IN_R3=269.98°; EVAP_OUT_A=2209 mm  [stored 7.24738 ft]; EVAP_OUT_R3=269.98°; FREON_IN_A=2209 mm  [stored 7.24738 ft]; FREON_IN_B=1290 mm  [stored 4.23228 ft]; FREON_IN_C=220 mm  [stored 0.721785 ft]; FREON_IN_Diametro=28 mm  [stored 0.0918635 ft]; FREON_IN_R3=269.98°; FREON_OUT_A=2209 mm  [stored 7.24738 ft]; FREON_OUT_B=1680 mm  [stored 5.51181 ft]; FREON_OUT_C=220 mm  [stored 0.721785 ft]; FREON_OUT_Diametro=42 mm  [stored 0.137795 ft]; FREON_OUT_R3=269.98°; F_Mid_STR6=795 mm  [stored 2.60827 ft]; F_OffSet=255 mm  [stored 0.836614 ft]; Frequency (Hz)=50; Is_STR5=Sì; Is_STR6=No; Lw (dBA)=83; Maximum current (A)=183.2; Nominal current (A)=129.8; PF_EN14511_W35W7 (kW)=0; PF_EN14511_tC50W7 (kW)=269.6; PR_EN14511_W45 (kW)=0; PT_EN14511_W7W45 (kW)=0; Psm_EN14511_W35W7 (kW)=0; QTc (m3/h)=0; Qc (m3/h)=0; Qe (m3/h)=46.4; Qr (m3/h)=0; REC_IN_A=2209 mm  [stored 7.24738 ft]; REC_IN_B=475 mm  [stored 1.5584 ft]; REC_IN_C=220 mm  [stored 0.721785 ft]; REC_IN_R3=269.98°; REC_OUT_A=2209 mm  [stored 7.24738 ft]; REC_OUT_B=865 mm  [stored 2.83793 ft]; REC_OUT_C=220 mm  [stored 0.721785 ft]; REC_OUT_R3=269.98°; RispettoD3=2209 mm  [stored 7.24738 ft]; SCOP_EN14825=0; SEER_EN14825=0; Starting current (A)=347.4; Type=CHILLER; Voltage (V)=400; Weight (kg)=1390; dPTc (kPa)=0; dPc (kPa)=0; dPe (kPa)=38; dPr (kPa)=0; n. poles=3+N
- TCEETU 4350: COND_IN_A=200 mm  [stored 0.656168 ft]; COND_IN_B=350 mm  [stored 1.14829 ft]; COND_IN_C=150 mm  [stored 0.492126 ft]; COND_IN_R3=0.00°; COND_OUT_A=200 mm  [stored 0.656168 ft]; COND_OUT_B=350 mm  [stored 1.14829 ft]; COND_OUT_C=200 mm  [stored 0.656168 ft]; COND_OUT_R3=0.00°; COP_EN14511_W7W45=0; DS_IN_A=2209 mm  [stored 7.24738 ft]; DS_IN_B=475 mm  [stored 1.5584 ft]; DS_IN_C=204 mm  [stored 0.669291 ft]; DS_IN_R3=269.98°; DS_OUT_A=2209 mm  [stored 7.24738 ft]; DS_OUT_B=725 mm  [stored 2.37861 ft]; DS_OUT_C=204 mm  [stored 0.669291 ft]; DS_OUT_R3=269.98°; EER_EN14511_W35W7=0; EER_EN14511_tC50W7=3.28; EVAP_IN_A=2209 mm  [stored 7.24738 ft]; EVAP_IN_R3=269.98°; EVAP_OUT_A=2209 mm  [stored 7.24738 ft]; EVAP_OUT_R3=269.98°; FREON_IN_A=2209 mm  [stored 7.24738 ft]; FREON_IN_B=1290 mm  [stored 4.23228 ft]; FREON_IN_C=220 mm  [stored 0.721785 ft]; FREON_IN_Diametro=28 mm  [stored 0.0918635 ft]; FREON_IN_R3=269.98°; FREON_OUT_A=2209 mm  [stored 7.24738 ft]; FREON_OUT_B=1680 mm  [stored 5.51181 ft]; FREON_OUT_C=220 mm  [stored 0.721785 ft]; FREON_OUT_Diametro=42 mm  [stored 0.137795 ft]; FREON_OUT_R3=269.98°; F_Mid_STR6=795 mm  [stored 2.60827 ft]; F_OffSet=255 mm  [stored 0.836614 ft]; Frequency (Hz)=50; Is_STR5=Sì; Is_STR6=No; Lw (dBA)=84; Maximum current (A)=216.4; Nominal current (A)=161.6; PF_EN14511_W35W7 (kW)=0; PF_EN14511_tC50W7 (kW)=309.9; PR_EN14511_W45 (kW)=0; PT_EN14511_W7W45 (kW)=0; Psm_EN14511_W35W7 (kW)=0; QTc (m3/h)=0; Qc (m3/h)=0; Qe (m3/h)=53.4; Qr (m3/h)=0; REC_IN_A=2209 mm  [stored 7.24738 ft]; REC_IN_B=475 mm  [stored 1.5584 ft]; REC_IN_C=220 mm  [stored 0.721785 ft]; REC_IN_R3=269.98°; REC_OUT_A=2209 mm  [stored 7.24738 ft]; REC_OUT_B=865 mm  [stored 2.83793 ft]; REC_OUT_C=220 mm  [stored 0.721785 ft]; REC_OUT_R3=269.98°; RispettoD3=2209 mm  [stored 7.24738 ft]; SCOP_EN14825=0; SEER_EN14825=0; Starting current (A)=480; Type=CHILLER; Voltage (V)=400; Weight (kg)=1430; dPTc (kPa)=0; dPc (kPa)=0; dPe (kPa)=36; dPr (kPa)=0; n. poles=3+N
- TCEETU 4395: COND_IN_A=200 mm  [stored 0.656168 ft]; COND_IN_B=350 mm  [stored 1.14829 ft]; COND_IN_C=150 mm  [stored 0.492126 ft]; COND_IN_R3=0.00°; COND_OUT_A=200 mm  [stored 0.656168 ft]; COND_OUT_B=350 mm  [stored 1.14829 ft]; COND_OUT_C=200 mm  [stored 0.656168 ft]; COND_OUT_R3=0.00°; COP_EN14511_W7W45=0; DS_IN_A=2209 mm  [stored 7.24738 ft]; DS_IN_B=475 mm  [stored 1.5584 ft]; DS_IN_C=204 mm  [stored 0.669291 ft]; DS_IN_R3=269.98°; DS_OUT_A=2209 mm  [stored 7.24738 ft]; DS_OUT_B=725 mm  [stored 2.37861 ft]; DS_OUT_C=204 mm  [stored 0.669291 ft]; DS_OUT_R3=269.98°; EER_EN14511_W35W7=0; EER_EN14511_tC50W7=3.28; EVAP_IN_A=2209 mm  [stored 7.24738 ft]; EVAP_IN_R3=269.98°; EVAP_OUT_A=2209 mm  [stored 7.24738 ft]; EVAP_OUT_R3=269.98°; FREON_IN_A=2209 mm  [stored 7.24738 ft]; FREON_IN_B=1290 mm  [stored 4.23228 ft]; FREON_IN_C=220 mm  [stored 0.721785 ft]; FREON_IN_Diametro=28 mm  [stored 0.0918635 ft]; FREON_IN_R3=269.98°; FREON_OUT_A=2209 mm  [stored 7.24738 ft]; FREON_OUT_B=1680 mm  [stored 5.51181 ft]; FREON_OUT_C=220 mm  [stored 0.721785 ft]; FREON_OUT_Diametro=42 mm  [stored 0.137795 ft]; FREON_OUT_R3=269.98°; F_Mid_STR6=795 mm  [stored 2.60827 ft]; F_OffSet=255 mm  [stored 0.836614 ft]; Frequency (Hz)=50; Is_STR5=Sì; Is_STR6=No; Lw (dBA)=85; Maximum current (A)=249.6; Nominal current (A)=193.5; PF_EN14511_W35W7 (kW)=0; PF_EN14511_tC50W7 (kW)=351.8; PR_EN14511_W45 (kW)=0; PT_EN14511_W7W45 (kW)=0; Psm_EN14511_W35W7 (kW)=0; QTc (m3/h)=0; Qc (m3/h)=0; Qe (m3/h)=60.6; Qr (m3/h)=0; REC_IN_A=2209 mm  [stored 7.24738 ft]; REC_IN_B=475 mm  [stored 1.5584 ft]; REC_IN_C=220 mm  [stored 0.721785 ft]; REC_IN_R3=269.98°; REC_OUT_A=2209 mm  [stored 7.24738 ft]; REC_OUT_B=865 mm  [stored 2.83793 ft]; REC_OUT_C=220 mm  [stored 0.721785 ft]; REC_OUT_R3=269.98°; RispettoD3=2209 mm  [stored 7.24738 ft]; SCOP_EN14825=0; SEER_EN14825=0; Starting current (A)=513.2; Type=CHILLER; Voltage (V)=400; Weight (kg)=1445; dPTc (kPa)=0; dPc (kPa)=0; dPe (kPa)=44; dPr (kPa)=0; n. poles=3+N
- WinFLOW_ECO_STR5: COND_IN_A=200 mm  [stored 0.656168 ft]; COND_IN_B=350 mm  [stored 1.14829 ft]; COND_IN_C=150 mm  [stored 0.492126 ft]; COND_IN_R3=0.00°; COND_OUT_A=200 mm  [stored 0.656168 ft]; COND_OUT_B=350 mm  [stored 1.14829 ft]; COND_OUT_C=200 mm  [stored 0.656168 ft]; COND_OUT_R3=0.00°; COP_EN14511_W7W45=0; DS_IN_A=200 mm  [stored 0.656168 ft]; DS_IN_B=475 mm  [stored 1.5584 ft]; DS_IN_C=204 mm  [stored 0.669291 ft]; DS_IN_R3=0.00°; DS_OUT_A=200 mm  [stored 0.656168 ft]; DS_OUT_B=725 mm  [stored 2.37861 ft]; DS_OUT_C=204 mm  [stored 0.669291 ft]; DS_OUT_R3=0.00°; EER_EN14511_W35W7=0; EER_EN14511_tC50W7=0; EVAP_IN_A=200 mm  [stored 0.656168 ft]; EVAP_IN_R3=0.00°; EVAP_OUT_A=200 mm  [stored 0.656168 ft]; EVAP_OUT_R3=0.00°; FREON_IN_A=200 mm  [stored 0.656168 ft]; FREON_IN_B=1290 mm  [stored 4.23228 ft]; FREON_IN_C=220 mm  [stored 0.721785 ft]; FREON_IN_Diametro=22 mm  [stored 0.0721785 ft]; FREON_IN_R3=0.00°; FREON_OUT_A=200 mm  [stored 0.656168 ft]; FREON_OUT_B=1680 mm  [stored 5.51181 ft]; FREON_OUT_C=220 mm  [stored 0.721785 ft]; FREON_OUT_Diametro=35 mm  [stored 0.114829 ft]; FREON_OUT_R3=0.00°; F_Mid_STR6=1463 mm  [stored 4.79987 ft]; F_OffSet=255 mm  [stored 0.836614 ft]; Frequency (Hz)=0; Is_STR5=Sì; Is_STR6=No; Lw (dBA)=79; Maximum current (A)=0; Nominal current (A)=0; PF_EN14511_W35W7 (kW)=0; PF_EN14511_tC50W7 (kW)=0; PR_EN14511_W45 (kW)=0; PT_EN14511_W7W45 (kW)=0; Psm_EN14511_W35W7 (kW)=0; QTc (m3/h)=0; Qc (m3/h)=0; Qe (m3/h)=0; Qr (m3/h)=0; REC_IN_A=200 mm  [stored 0.656168 ft]; REC_IN_B=475 mm  [stored 1.5584 ft]; REC_IN_C=220 mm  [stored 0.721785 ft]; REC_IN_R3=0.00°; REC_OUT_A=200 mm  [stored 0.656168 ft]; REC_OUT_B=865 mm  [stored 2.83793 ft]; REC_OUT_C=220 mm  [stored 0.721785 ft]; REC_OUT_R3=0.00°; RispettoD3=2209 mm  [stored 7.24738 ft]; SCOP_EN14825=0; SEER_EN14825=0; Starting current (A)=0; Type=CHILLER; Voltage (V)=0; Weight (kg)=1040; dPTc (kPa)=0; dPc (kPa)=0; dPe (kPa)=0; dPr (kPa)=0; n. poles=0
- WinFLOW_ECO_STR6: COND_IN_A=200 mm  [stored 0.656168 ft]; COND_IN_B=350 mm  [stored 1.14829 ft]; COND_IN_C=150 mm  [stored 0.492126 ft]; COND_IN_R3=0.00°; COND_OUT_A=200 mm  [stored 0.656168 ft]; COND_OUT_B=350 mm  [stored 1.14829 ft]; COND_OUT_C=200 mm  [stored 0.656168 ft]; COND_OUT_R3=0.00°; COP_EN14511_W7W45=0; DS_IN_A=200 mm  [stored 0.656168 ft]; DS_IN_B=475 mm  [stored 1.5584 ft]; DS_IN_C=204 mm  [stored 0.669291 ft]; DS_IN_R3=0.00°; DS_OUT_A=200 mm  [stored 0.656168 ft]; DS_OUT_B=725 mm  [stored 2.37861 ft]; DS_OUT_C=204 mm  [stored 0.669291 ft]; DS_OUT_R3=0.00°; EER_EN14511_W35W7=0; EER_EN14511_tC50W7=0; EVAP_IN_A=200 mm  [stored 0.656168 ft]; EVAP_IN_R3=0.00°; EVAP_OUT_A=200 mm  [stored 0.656168 ft]; EVAP_OUT_R3=0.00°; FREON_IN_A=200 mm  [stored 0.656168 ft]; FREON_IN_B=1290 mm  [stored 4.23228 ft]; FREON_IN_C=220 mm  [stored 0.721785 ft]; FREON_IN_Diametro=22 mm  [stored 0.0721785 ft]; FREON_IN_R3=0.00°; FREON_OUT_A=200 mm  [stored 0.656168 ft]; FREON_OUT_B=1680 mm  [stored 5.51181 ft]; FREON_OUT_C=220 mm  [stored 0.721785 ft]; FREON_OUT_Diametro=35 mm  [stored 0.114829 ft]; FREON_OUT_R3=0.00°; F_Mid_STR6=1463 mm  [stored 4.79987 ft]; F_OffSet=491 mm  [stored 1.61089 ft]; Frequency (Hz)=0; Is_STR5=No; Is_STR6=Sì; Lw (dBA)=79; Maximum current (A)=0; Nominal current (A)=0; PF_EN14511_W35W7 (kW)=0; PF_EN14511_tC50W7 (kW)=0; PR_EN14511_W45 (kW)=0; PT_EN14511_W7W45 (kW)=0; Psm_EN14511_W35W7 (kW)=0; QTc (m3/h)=0; Qc (m3/h)=0; Qe (m3/h)=0; Qr (m3/h)=0; REC_IN_A=200 mm  [stored 0.656168 ft]; REC_IN_B=475 mm  [stored 1.5584 ft]; REC_IN_C=220 mm  [stored 0.721785 ft]; REC_IN_R3=0.00°; REC_OUT_A=200 mm  [stored 0.656168 ft]; REC_OUT_B=865 mm  [stored 2.83793 ft]; REC_OUT_C=220 mm  [stored 0.721785 ft]; REC_OUT_R3=0.00°; RispettoD3=3434 mm  [stored 11.2664 ft]; SCOP_EN14825=0; SEER_EN14825=0; Starting current (A)=0; Type=CHILLER; Voltage (V)=0; Weight (kg)=1040; dPTc (kPa)=0; dPc (kPa)=0; dPe (kPa)=0; dPr (kPa)=0; n. poles=0

note: [stored X ft] marks values corroborated as IEEE doubles in the binary element streams (Revit-internal decimal feet)
